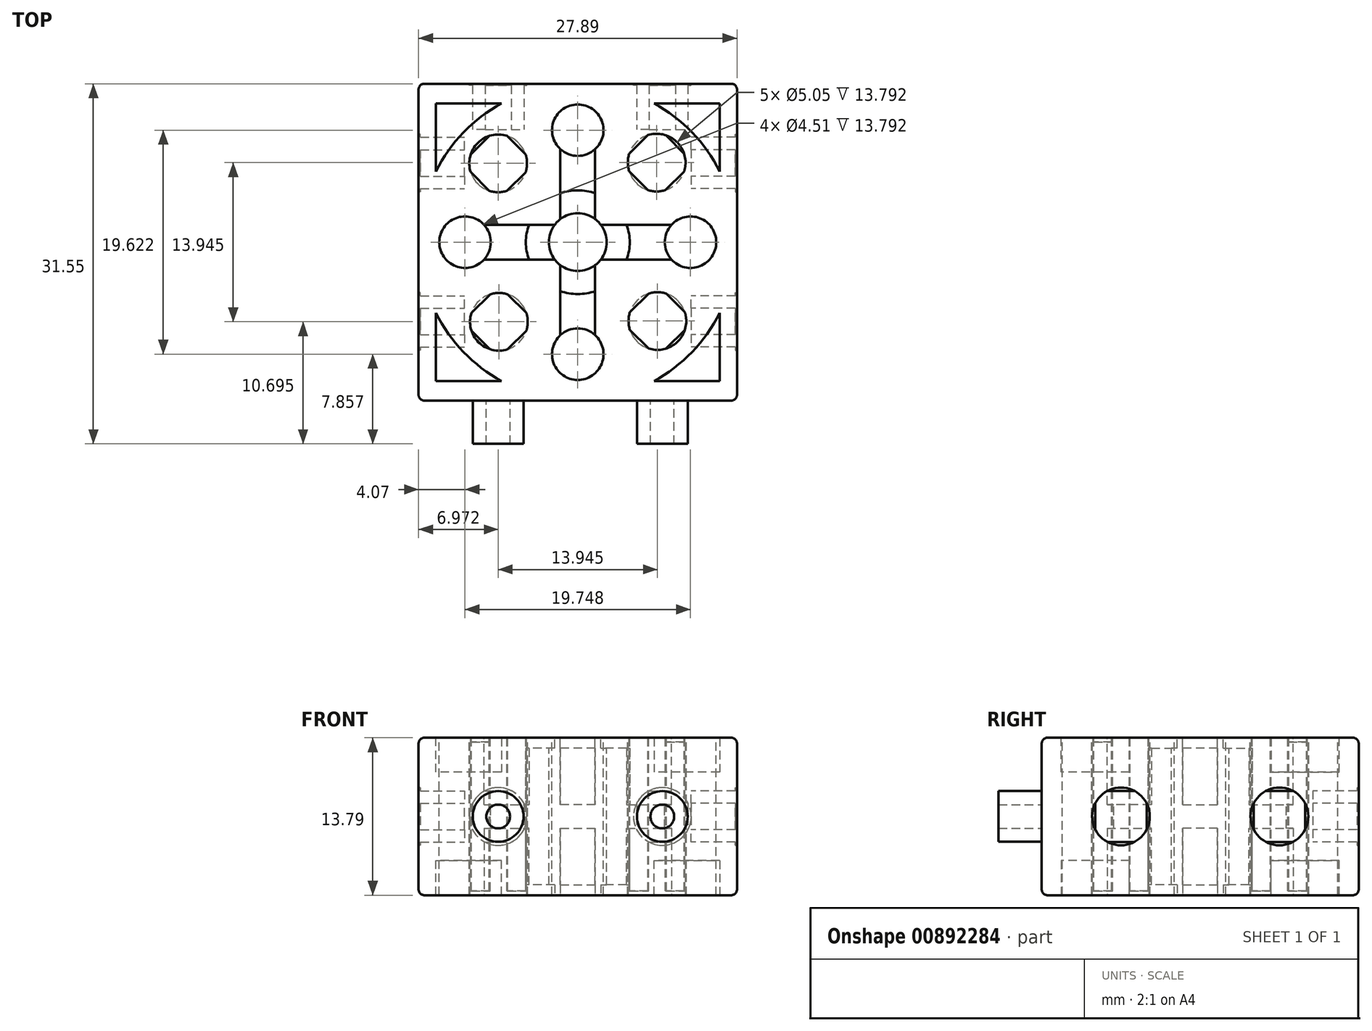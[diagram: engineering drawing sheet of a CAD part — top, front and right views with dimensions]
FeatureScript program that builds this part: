
annotation { "Feature Type Name" : "Feature", "Feature Type Description" : "" }
export const myFeature = defineFeature(function(context is Context, id is Id, definition is map)
    precondition{}
    {
        {
            var Q0;
            Q0=qCreatedBy(makeId("Top.planeOp"),FACE);
            var sketch = newSketch(context, id + "F0", { "sketchPlane" : qUnion([Q0])});
            skLineSegment(sketch, "E0.bottom", {"start": v(-12.61, 9.27) * mm, "end": v(15.28, 9.27) * mm});
            skLineSegment(sketch, "E0.top", {"start": v(-12.61, -18.5) * mm, "end": v(15.28, -18.5) * mm});
            skLineSegment(sketch, "E0.left", {"start": v(-12.61, 9.27) * mm, "end": v(-12.61, -18.5) * mm});
            skLineSegment(sketch, "E0.right", {"start": v(15.28, 9.27) * mm, "end": v(15.28, -18.5) * mm});
            skSolve(sketch);
        }
        {
            var Q0;
            Q0=qSketchRegion(id+"F0",true);
            extrude(context, id + "F1", {"entities" : qUnion([Q0]), "depth" : 13.8 * mm, "offsetDistance" : 25.4 * mm});
        }
        {
            var Q0;
            Q0=makeQuery(id+"F1.opExtrude","CAP_FACE",FACE,{"disambiguationData":[OSD([sQuery(id+"F0.wireOp",EDGE,"E0.bottom"),sQuery(id+"F0.wireOp",EDGE,"E0.top"),sQuery(id+"F0.wireOp",EDGE,"E0.left"),sQuery(id+"F0.wireOp",EDGE,"E0.right")])],"isStart":false});
            var sketch = newSketch(context, id + "F2", { "sketchPlane" : qUnion([Q0])});
            skLineSegment(sketch, "E1", {"start": v(1.33, 9.27) * mm, "end": v(1.33, -18.5) * mm, "construction": true});
            skLineSegment(sketch, "E2", {"start": v(-12.61, -4.61) * mm, "end": v(15.28, -4.61) * mm, "construction": true});
            skLineSegment(sketch, "E3.bottom", {"start": v(13.75, 7.56) * mm, "end": v(-11.09, 7.56) * mm});
            skLineSegment(sketch, "E3.top", {"start": v(13.75, -16.78) * mm, "end": v(-11.09, -16.78) * mm});
            skLineSegment(sketch, "E3.left", {"start": v(13.75, 7.56) * mm, "end": v(13.75, -16.78) * mm});
            skLineSegment(sketch, "E3.right", {"start": v(-11.09, 7.56) * mm, "end": v(-11.09, -16.78) * mm});
            skPoint(sketch, "E3.middle", {"position": v(1.33, -4.61) * mm});
            skSolve(sketch);
        }
        {
            var Q0;
            Q0=qSketchRegion(id+"F2",true);
            extrude(context, id + "F3", {"entities" : qUnion([Q0]), "operationType" : NewBodyOperationType.REMOVE, "oppositeDirection" : true, "depth" : 3.02 * mm, "offsetDistance" : 25.4 * mm});
        }
        {
            var Q0;
            Q0=makeQuery(id+"F1.opExtrude","CAP_FACE",FACE,{"disambiguationData":[OSD([sQuery(id+"F0.wireOp",EDGE,"E0.bottom"),sQuery(id+"F0.wireOp",EDGE,"E0.top"),sQuery(id+"F0.wireOp",EDGE,"E0.left"),sQuery(id+"F0.wireOp",EDGE,"E0.right")])],"isStart":true});
            var sketch = newSketch(context, id + "F4", { "sketchPlane" : qUnion([Q0])});
            skLineSegment(sketch, "E4.bottom", {"start": v(-11.09, -7.56) * mm, "end": v(13.75, -7.56) * mm});
            skLineSegment(sketch, "E4.top", {"start": v(-11.09, 16.78) * mm, "end": v(13.75, 16.78) * mm});
            skLineSegment(sketch, "E4.left", {"start": v(-11.09, -7.56) * mm, "end": v(-11.09, 16.78) * mm});
            skLineSegment(sketch, "E4.right", {"start": v(13.75, -7.56) * mm, "end": v(13.75, 16.78) * mm});
            skSolve(sketch);
        }
        {
            var Q0;
            Q0=makeQuery(id+"F4.imprint","IMPRINT",FACE,{"disambiguationData":[TD([[makeQuery(id+"F4.imprint","IMPRINT",EDGE,{"derivedFrom":sQuery(id+"F4.wireOp",EDGE,"E4.bottom")}),1.0]])]});
            extrude(context, id + "F5", {"entities" : qUnion([Q0]), "operationType" : NewBodyOperationType.REMOVE, "oppositeDirection" : true, "depth" : 3.02 * mm, "offsetDistance" : 25.4 * mm});
        }
        {
            var Q0;
            Q0=makeQuery(id+"F5.boolean.opBoolean","COPY",FACE,{"derivedFrom":makeQuery(id+"F5.opExtrude","CAP_FACE",FACE,{"disambiguationData":[OSD([sQuery(id+"F4.wireOp",EDGE,"E4.bottom"),sQuery(id+"F4.wireOp",EDGE,"E4.top"),sQuery(id+"F4.wireOp",EDGE,"E4.left"),sQuery(id+"F4.wireOp",EDGE,"E4.right")])],"isStart":false})});
            var sketch = newSketch(context, id + "F6", { "sketchPlane" : qUnion([Q0])});
            skCircle(sketch, "E5", {"center": v(1.33, 4.61) * mm, "radius": 13.88 * mm});
            skLineSegment(sketch, "E6", {"start": v(1.33, -7.56) * mm, "end": v(1.33, 16.78) * mm, "construction": true});
            skPoint(sketch, "E6.startSnap0", {"position": v(1.33, -7.56) * mm});
            skSolve(sketch);
        }
        {
            var Q0;
            {var subQ0=sQuery(id+"F6.wireOp",EDGE,"E5");var subQ1=makeQuery(id+"F5.boolean.opBoolean","COPY",EDGE,{"derivedFrom":makeQuery(id+"F5.opExtrude","CAP_EDGE",EDGE,{"disambiguationData":[OSD([sQuery(id+"F4.wireOp",EDGE,"E4.top")])],"isStart":false})});var subQ2=makeQuery(id+"F6.imprint","INTERSECT",VERTEX,{"disambiguationData":[OD(0.0)],"derivedFrom":[subQ1,subQ0]});Q0=makeQuery(id+"F6.imprint","IMPRINT",FACE,{"disambiguationData":[TD([[makeQuery(id+"F6.imprint","IMPRINT",EDGE,{"disambiguationData":[TD([[subQ2,-1.0]])],"derivedFrom":subQ0}),1.0]])]});}
            var Q1;
            {var subQ0=sQuery(id+"F6.wireOp",EDGE,"E5");var subQ1=makeQuery(id+"F5.boolean.opBoolean","COPY",EDGE,{"derivedFrom":makeQuery(id+"F5.opExtrude","CAP_EDGE",EDGE,{"disambiguationData":[OSD([sQuery(id+"F4.wireOp",EDGE,"E4.left")])],"isStart":false})});var subQ2=makeQuery(id+"F6.imprint","INTERSECT",VERTEX,{"disambiguationData":[OD(0.0)],"derivedFrom":[subQ1,subQ0]});Q1=makeQuery(id+"F6.imprint","IMPRINT",FACE,{"disambiguationData":[TD([[makeQuery(id+"F6.imprint","IMPRINT",EDGE,{"disambiguationData":[TD([[subQ2,-1.0]])],"derivedFrom":subQ0}),1.0]])]});}
            var Q2;
            {var subQ0=sQuery(id+"F6.wireOp",EDGE,"E5");var subQ1=makeQuery(id+"F5.boolean.opBoolean","COPY",EDGE,{"derivedFrom":makeQuery(id+"F5.opExtrude","CAP_EDGE",EDGE,{"disambiguationData":[OSD([sQuery(id+"F4.wireOp",EDGE,"E4.bottom")])],"isStart":false})});var subQ2=makeQuery(id+"F6.imprint","INTERSECT",VERTEX,{"disambiguationData":[OD(0.0)],"derivedFrom":[subQ1,subQ0]});Q2=makeQuery(id+"F6.imprint","IMPRINT",FACE,{"disambiguationData":[TD([[makeQuery(id+"F6.imprint","IMPRINT",EDGE,{"disambiguationData":[TD([[subQ2,-1.0]])],"derivedFrom":subQ0}),1.0]])]});}
            var Q3;
            {var subQ0=sQuery(id+"F6.wireOp",EDGE,"E5");var subQ1=makeQuery(id+"F5.boolean.opBoolean","COPY",EDGE,{"derivedFrom":makeQuery(id+"F5.opExtrude","CAP_EDGE",EDGE,{"disambiguationData":[OSD([sQuery(id+"F4.wireOp",EDGE,"E4.right")])],"isStart":false})});var subQ2=makeQuery(id+"F6.imprint","INTERSECT",VERTEX,{"disambiguationData":[OD(0.0)],"derivedFrom":[subQ1,subQ0]});Q3=makeQuery(id+"F6.imprint","IMPRINT",FACE,{"disambiguationData":[TD([[makeQuery(id+"F6.imprint","IMPRINT",EDGE,{"disambiguationData":[TD([[subQ2,1.0]])],"derivedFrom":subQ0}),1.0]])]});}
            var Q4;
            {var subQ0=sQuery(id+"F6.wireOp",EDGE,"E5");var subQ8=makeQuery(id+"F5.boolean.opBoolean","COPY",EDGE,{"derivedFrom":makeQuery(id+"F5.opExtrude","CAP_EDGE",EDGE,{"disambiguationData":[OSD([sQuery(id+"F4.wireOp",EDGE,"E4.top")])],"isStart":false})});var subQ11=makeQuery(id+"F6.imprint","INTERSECT",VERTEX,{"disambiguationData":[OD(0.0)],"derivedFrom":[subQ8,subQ0]});Q4=makeQuery(id+"F6.imprint","IMPRINT",FACE,{"disambiguationData":[TD([[makeQuery(id+"F6.imprint","IMPRINT",EDGE,{"disambiguationData":[TD([[subQ11,1.0]])],"derivedFrom":subQ0}),1.0]])]});}
            extrude(context, id + "F7", {"entities" : qUnion([Q0, Q1, Q2, Q3, Q4]), "operationType" : NewBodyOperationType.ADD, "depth" : 3.02 * mm, "offsetDistance" : 25.4 * mm});
        }
        {
            var Q0;
            Q0=makeQuery(id+"F3.boolean.opBoolean","COPY",FACE,{"derivedFrom":makeQuery(id+"F3.opExtrude","CAP_FACE",FACE,{"disambiguationData":[OSD([sQuery(id+"F2.wireOp",EDGE,"E3.bottom"),sQuery(id+"F2.wireOp",EDGE,"E3.top"),sQuery(id+"F2.wireOp",EDGE,"E3.left"),sQuery(id+"F2.wireOp",EDGE,"E3.right")])],"isStart":false})});
            var sketch = newSketch(context, id + "F8", { "sketchPlane" : qUnion([Q0])});
            skLineSegment(sketch, "E7", {"start": v(1.33, 7.56) * mm, "end": v(1.33, -16.78) * mm, "construction": true});
            skCircle(sketch, "E8", {"center": v(1.33, -4.61) * mm, "radius": 13.88 * mm});
            skSolve(sketch);
        }
        {
            var Q0;
            Q0=qSketchRegion(id+"F8",true);
            extrude(context, id + "F9", {"entities" : qUnion([Q0]), "operationType" : NewBodyOperationType.ADD, "depth" : 3.02 * mm, "offsetDistance" : 25.4 * mm});
        }
        {
            var Q0;
            Q0=makeQuery(id+"F9.boolean.opBoolean","MERGE",FACE,{"derivedFrom":[makeQuery(id+"F1.opExtrude","CAP_FACE",FACE,{"disambiguationData":[OSD([sQuery(id+"F0.wireOp",EDGE,"E0.bottom"),sQuery(id+"F0.wireOp",EDGE,"E0.top"),sQuery(id+"F0.wireOp",EDGE,"E0.left"),sQuery(id+"F0.wireOp",EDGE,"E0.right")])],"isStart":false}),makeQuery(id+"F9.opExtrude","CAP_FACE",FACE,{"disambiguationData":[OSD([sQuery(id+"F8.wireOp",EDGE,"E8")])],"isStart":false})]});
            var sketch = newSketch(context, id + "F10", { "sketchPlane" : qUnion([Q0])});
            skLineSegment(sketch, "E9", {"start": v(-12.61, -4.61) * mm, "end": v(15.28, -4.61) * mm, "construction": true});
            skLineSegment(sketch, "E10", {"start": v(1.33, 9.27) * mm, "end": v(1.33, -18.5) * mm, "construction": true});
            skCircle(sketch, "E11", {"center": v(1.33, -4.61) * mm, "radius": 2.53 * mm});
            skCircle(sketch, "E12", {"center": v(1.33, -14.42) * mm, "radius": 2.25 * mm});
            skCircle(sketch, "E13", {"center": v(1.33, 5.2) * mm, "radius": 2.25 * mm});
            skCircle(sketch, "E14", {"center": v(-8.54, -4.61) * mm, "radius": 2.25 * mm});
            skCircle(sketch, "E15", {"center": v(11.2, -4.61) * mm, "radius": 2.25 * mm});
            skCircle(sketch, "E16", {"center": v(-5.64, 2.3) * mm, "radius": 2.53 * mm});
            skCircle(sketch, "E17.1.0", {"center": v(-5.57, -11.58) * mm, "radius": 2.53 * mm});
            skCircle(sketch, "E17.2.0", {"center": v(8.3, -11.52) * mm, "radius": 2.53 * mm});
            skCircle(sketch, "E17.3.0", {"center": v(8.24, 2.36) * mm, "radius": 2.53 * mm});
            skSolve(sketch);
        }
        {
            var Q0;
            Q0=qSketchRegion(id+"F10",true);
            extrude(context, id + "F11", {"entities" : qUnion([Q0]), "operationType" : NewBodyOperationType.REMOVE, "oppositeDirection" : true, "depth" : 25.4 * mm, "offsetDistance" : 25.4 * mm});
        }
        {
            var Q0;
            Q0=makeQuery(id+"F9.boolean.opBoolean","MERGE",FACE,{"derivedFrom":[makeQuery(id+"F1.opExtrude","CAP_FACE",FACE,{"disambiguationData":[OSD([sQuery(id+"F0.wireOp",EDGE,"E0.bottom"),sQuery(id+"F0.wireOp",EDGE,"E0.top"),sQuery(id+"F0.wireOp",EDGE,"E0.left"),sQuery(id+"F0.wireOp",EDGE,"E0.right")])],"isStart":false}),makeQuery(id+"F9.opExtrude","CAP_FACE",FACE,{"disambiguationData":[OSD([sQuery(id+"F8.wireOp",EDGE,"E8")])],"isStart":false})]});
            var sketch = newSketch(context, id + "F12", { "sketchPlane" : qUnion([Q0])});
            skLineSegment(sketch, "E18", {"start": v(-12.61, -4.61) * mm, "end": v(15.28, -4.61) * mm, "construction": true});
            skLineSegment(sketch, "E19", {"start": v(1.33, 9.27) * mm, "end": v(1.33, -18.5) * mm, "construction": true});
            skLineSegment(sketch, "E20", {"start": v(-6.88, -3.09) * mm, "end": v(9.55, -3.09) * mm});
            skLineSegment(sketch, "E21", {"start": v(-6.88, -6.14) * mm, "end": v(9.55, -6.14) * mm});
            skLineSegment(sketch, "E22", {"start": v(-0.19, 3.54) * mm, "end": v(-0.19, -12.76) * mm});
            skLineSegment(sketch, "E23", {"start": v(2.86, -12.76) * mm, "end": v(2.86, 3.54) * mm});
            skLineSegment(sketch, "E24", {"start": v(-0.19, -7.96) * mm, "end": v(2.86, -7.96) * mm, "construction": true});
            skPoint(sketch, "E25", {"position": v(1.33, -7.96) * mm});
            skLineSegment(sketch, "E26", {"start": v(-2, -3.09) * mm, "end": v(-2, -6.14) * mm, "construction": true});
            skPoint(sketch, "E27", {"position": v(-2, -4.61) * mm});
            skSolve(sketch);
        }
        {
            var Q0;
            {var subQ0=sQuery(id+"F12.wireOp",EDGE,"E22");var subQ1=makeQuery(id+"F11.boolean.opBoolean","COPY",EDGE,{"derivedFrom":makeQuery(id+"F11.opExtrude","CAP_EDGE",EDGE,{"disambiguationData":[OSD([sQuery(id+"F10.wireOp",EDGE,"E13")])],"isStart":true})});var subQ2=makeQuery(id+"F12.imprint","INTERSECT",VERTEX,{"derivedFrom":[subQ1,subQ0]});Q0=makeQuery(id+"F12.imprint","IMPRINT",FACE,{"disambiguationData":[TD([[makeQuery(id+"F12.imprint","IMPRINT",EDGE,{"disambiguationData":[TD([[subQ2,-1.0]])],"derivedFrom":subQ0}),1.0]])]});}
            var Q1;
            {var subQ0=sQuery(id+"F12.wireOp",EDGE,"E22");var subQ1=makeQuery(id+"F11.boolean.opBoolean","COPY",EDGE,{"derivedFrom":makeQuery(id+"F11.opExtrude","CAP_EDGE",EDGE,{"disambiguationData":[OSD([sQuery(id+"F10.wireOp",EDGE,"E12")])],"isStart":true})});var subQ2=makeQuery(id+"F12.imprint","INTERSECT",VERTEX,{"derivedFrom":[subQ1,subQ0]});Q1=makeQuery(id+"F12.imprint","IMPRINT",FACE,{"disambiguationData":[TD([[makeQuery(id+"F12.imprint","IMPRINT",EDGE,{"disambiguationData":[TD([[subQ2,1.0]])],"derivedFrom":subQ0}),1.0]])]});}
            var Q2;
            {var subQ0=sQuery(id+"F12.wireOp",EDGE,"E20");var subQ1=makeQuery(id+"F11.boolean.opBoolean","COPY",EDGE,{"derivedFrom":makeQuery(id+"F11.opExtrude","CAP_EDGE",EDGE,{"disambiguationData":[OSD([sQuery(id+"F10.wireOp",EDGE,"E14")])],"isStart":true})});var subQ2=makeQuery(id+"F12.imprint","INTERSECT",VERTEX,{"derivedFrom":[subQ1,subQ0]});Q2=makeQuery(id+"F12.imprint","IMPRINT",FACE,{"disambiguationData":[TD([[makeQuery(id+"F12.imprint","IMPRINT",EDGE,{"disambiguationData":[TD([[subQ2,-1.0]])],"derivedFrom":subQ0}),-1.0]])]});}
            var Q3;
            {var subQ0=sQuery(id+"F12.wireOp",EDGE,"E20");var subQ1=makeQuery(id+"F11.boolean.opBoolean","COPY",EDGE,{"derivedFrom":makeQuery(id+"F11.opExtrude","CAP_EDGE",EDGE,{"disambiguationData":[OSD([sQuery(id+"F10.wireOp",EDGE,"E15")])],"isStart":true})});var subQ2=makeQuery(id+"F12.imprint","INTERSECT",VERTEX,{"derivedFrom":[subQ1,subQ0]});Q3=makeQuery(id+"F12.imprint","IMPRINT",FACE,{"disambiguationData":[TD([[makeQuery(id+"F12.imprint","IMPRINT",EDGE,{"disambiguationData":[TD([[subQ2,1.0]])],"derivedFrom":subQ0}),-1.0]])]});}
            extrude(context, id + "F13", {"entities" : qUnion([Q0, Q1, Q2, Q3]), "operationType" : NewBodyOperationType.REMOVE, "oppositeDirection" : true, "depth" : 5.87 * mm, "offsetDistance" : 25.4 * mm});
        }
        {
            var Q0;
            Q0=makeQuery(id+"F7.boolean.opBoolean","MERGE",FACE,{"derivedFrom":[makeQuery(id+"F1.opExtrude","CAP_FACE",FACE,{"disambiguationData":[OSD([sQuery(id+"F0.wireOp",EDGE,"E0.bottom"),sQuery(id+"F0.wireOp",EDGE,"E0.top"),sQuery(id+"F0.wireOp",EDGE,"E0.left"),sQuery(id+"F0.wireOp",EDGE,"E0.right")])],"isStart":true}),makeQuery(id+"F7.opExtrude","CAP_FACE",FACE,{"disambiguationData":[OSD([sQuery(id+"F6.wireOp",EDGE,"E5")])],"isStart":false})]});
            var sketch = newSketch(context, id + "F14", { "sketchPlane" : qUnion([Q0])});
            skLineSegment(sketch, "E28.0", {"start": v(2.86, 12.76) * mm, "end": v(2.86, 6.63) * mm});
            skLineSegment(sketch, "E28.1", {"start": v(3.35, 6.14) * mm, "end": v(9.55, 6.14) * mm});
            skLineSegment(sketch, "E28.2", {"start": v(3.35, 3.09) * mm, "end": v(9.55, 3.09) * mm});
            skLineSegment(sketch, "E28.3", {"start": v(2.86, 2.6) * mm, "end": v(2.86, -3.54) * mm});
            skLineSegment(sketch, "E28.4", {"start": v(-0.19, -3.54) * mm, "end": v(-0.19, 2.6) * mm});
            skLineSegment(sketch, "E28.5", {"start": v(-0.19, 6.63) * mm, "end": v(-0.19, 12.76) * mm});
            skLineSegment(sketch, "E28.6", {"start": v(-6.88, 6.14) * mm, "end": v(-0.68, 6.14) * mm});
            skLineSegment(sketch, "E28.7", {"start": v(-6.88, 3.09) * mm, "end": v(-0.68, 3.09) * mm});
            skSolve(sketch);
        }
        {
            var Q0;
            {var subQ0=sQuery(id+"F14.wireOp",EDGE,"E28.6");Q0=makeQuery(id+"F14.imprint","IMPRINT",FACE,{"disambiguationData":[TD([[makeQuery(id+"F14.imprint","IMPRINT",EDGE,{"derivedFrom":subQ0}),-1.0]])]});}
            var Q1;
            {var subQ0=sQuery(id+"F14.wireOp",EDGE,"E28.3");Q1=makeQuery(id+"F14.imprint","IMPRINT",FACE,{"disambiguationData":[TD([[makeQuery(id+"F14.imprint","IMPRINT",EDGE,{"derivedFrom":subQ0}),-1.0]])]});}
            var Q2;
            {var subQ0=sQuery(id+"F14.wireOp",EDGE,"E28.0");Q2=makeQuery(id+"F14.imprint","IMPRINT",FACE,{"disambiguationData":[TD([[makeQuery(id+"F14.imprint","IMPRINT",EDGE,{"derivedFrom":subQ0}),-1.0]])]});}
            var Q3;
            {var subQ0=sQuery(id+"F14.wireOp",EDGE,"E28.1");Q3=makeQuery(id+"F14.imprint","IMPRINT",FACE,{"disambiguationData":[TD([[makeQuery(id+"F14.imprint","IMPRINT",EDGE,{"derivedFrom":subQ0}),-1.0]])]});}
            extrude(context, id + "F15", {"entities" : qUnion([Q0, Q1, Q2, Q3]), "operationType" : NewBodyOperationType.REMOVE, "oppositeDirection" : true, "depth" : 5.87 * mm, "offsetDistance" : 25.4 * mm});
        }
        {
            var Q0;
            Q0=makeQuery(id+"F15.boolean.opBoolean","COPY",FACE,{"derivedFrom":makeQuery(id+"F15.opExtrude","CAP_FACE",FACE,{"disambiguationData":[OSD([sQuery(id+"F0.wireOp",EDGE,"E0.bottom"),sQuery(id+"F0.wireOp",EDGE,"E0.top"),sQuery(id+"F0.wireOp",EDGE,"E0.left"),sQuery(id+"F0.wireOp",EDGE,"E0.right"),sQuery(id+"F6.wireOp",EDGE,"E5"),sQuery(id+"F10.wireOp",EDGE,"E11"),sQuery(id+"F10.wireOp",EDGE,"E13"),sQuery(id+"F14.wireOp",EDGE,"E28.3"),sQuery(id+"F14.wireOp",EDGE,"E28.4")])],"isStart":false})});
            var sketch = newSketch(context, id + "F16", { "sketchPlane" : qUnion([Q0])});
            skCircle(sketch, "E29", {"center": v(1.33, 4.61) * mm, "radius": 4.55 * mm});
            skCircle(sketch, "E30", {"center": v(1.33, 4.61) * mm, "radius": 2.53 * mm});
            skSolve(sketch);
        }
        {
            var Q0;
            {var subQ5=sQuery(id+"F16.wireOp",EDGE,"E30");Q0=makeQuery(id+"F16.imprint","IMPRINT",FACE,{"disambiguationData":[TD([[makeQuery(id+"F16.imprint","IMPRINT",EDGE,{"disambiguationData":[OD(1.0)],"derivedFrom":subQ5}),-1.0]])]});}
            var Q1;
            {var subQ5=sQuery(id+"F16.wireOp",EDGE,"E30");Q1=makeQuery(id+"F16.imprint","IMPRINT",FACE,{"disambiguationData":[TD([[makeQuery(id+"F16.imprint","IMPRINT",EDGE,{"disambiguationData":[OD(0.0)],"derivedFrom":subQ5}),1.0]])]});}
            extrude(context, id + "F17", {"entities" : qUnion([Q0, Q1]), "operationType" : NewBodyOperationType.ADD, "depth" : 4.95 * mm, "offsetDistance" : 25.4 * mm});
        }
        {
            var Q0;
            Q0=makeQuery(id+"F13.boolean.opBoolean","COPY",FACE,{"derivedFrom":makeQuery(id+"F13.opExtrude","CAP_FACE",FACE,{"disambiguationData":[OSD([sQuery(id+"F10.wireOp",EDGE,"E11"),sQuery(id+"F10.wireOp",EDGE,"E12"),sQuery(id+"F12.wireOp",EDGE,"E22"),sQuery(id+"F12.wireOp",EDGE,"E23")])],"isStart":false})});
            var sketch = newSketch(context, id + "F18", { "sketchPlane" : qUnion([Q0])});
            skCircle(sketch, "E31", {"center": v(1.33, -4.61) * mm, "radius": 4.55 * mm});
            skCircle(sketch, "E32", {"center": v(1.33, -4.61) * mm, "radius": 2.53 * mm});
            skSolve(sketch);
        }
        {
            var Q0;
            {var subQ0=sQuery(id+"F18.wireOp",EDGE,"E31");var subQ1=sQuery(id+"F12.wireOp",EDGE,"E22");var subQ2=makeQuery(id+"F11.boolean.opBoolean","COPY",EDGE,{"derivedFrom":makeQuery(id+"F11.opExtrude","CAP_EDGE",EDGE,{"disambiguationData":[OSD([sQuery(id+"F10.wireOp",EDGE,"E12")])],"isStart":true})});var subQ4=makeQuery(id+"F13.boolean.opBoolean","COPY",EDGE,{"derivedFrom":makeQuery(id+"F13.opExtrude","CAP_EDGE",EDGE,{"disambiguationData":[OSD([subQ1]),TDD([makeQuery(id+"F12.imprint","IMPRINT",EDGE,{"disambiguationData":[TD([[makeQuery(id+"F12.imprint","INTERSECT",VERTEX,{"derivedFrom":[subQ2,subQ1]}),1.0]])],"derivedFrom":subQ1})])],"isStart":false})});var subQ5=makeQuery(id+"F18.imprint","INTERSECT",VERTEX,{"derivedFrom":[subQ4,subQ0]});Q0=makeQuery(id+"F18.imprint","IMPRINT",FACE,{"disambiguationData":[TD([[makeQuery(id+"F18.imprint","IMPRINT",EDGE,{"disambiguationData":[TD([[subQ5,1.0]])],"derivedFrom":subQ0}),1.0]])]});}
            var Q1;
            {var subQ0=sQuery(id+"F18.wireOp",EDGE,"E31");var subQ1=sQuery(id+"F12.wireOp",EDGE,"E22");var subQ2=makeQuery(id+"F11.boolean.opBoolean","COPY",EDGE,{"derivedFrom":makeQuery(id+"F11.opExtrude","CAP_EDGE",EDGE,{"disambiguationData":[OSD([sQuery(id+"F10.wireOp",EDGE,"E12")])],"isStart":true})});var subQ4=makeQuery(id+"F13.boolean.opBoolean","COPY",EDGE,{"derivedFrom":makeQuery(id+"F13.opExtrude","CAP_EDGE",EDGE,{"disambiguationData":[OSD([subQ1]),TDD([makeQuery(id+"F12.imprint","IMPRINT",EDGE,{"disambiguationData":[TD([[makeQuery(id+"F12.imprint","INTERSECT",VERTEX,{"derivedFrom":[subQ2,subQ1]}),1.0]])],"derivedFrom":subQ1})])],"isStart":false})});var subQ5=makeQuery(id+"F18.imprint","INTERSECT",VERTEX,{"derivedFrom":[subQ4,subQ0]});Q1=makeQuery(id+"F18.imprint","IMPRINT",FACE,{"disambiguationData":[TD([[makeQuery(id+"F18.imprint","IMPRINT",EDGE,{"disambiguationData":[TD([[subQ5,-1.0]])],"derivedFrom":subQ0}),1.0]])]});}
            extrude(context, id + "F19", {"entities" : qUnion([Q0, Q1]), "operationType" : NewBodyOperationType.ADD, "depth" : 4.95 * mm, "offsetDistance" : 25.4 * mm});
        }
        {
            var Q0;
            Q0=makeQuery(id+"F1.opExtrude","SWEPT_FACE",FACE,{"disambiguationData":[OSD([sQuery(id+"F0.wireOp",EDGE,"E0.top")])]});
            var sketch = newSketch(context, id + "F20", { "sketchPlane" : qUnion([Q0])});
            skLineSegment(sketch, "E33", {"start": v(15.28, 6.9) * mm, "end": v(-12.61, 6.9) * mm, "construction": true});
            skCircle(sketch, "E34", {"center": v(8.74, 6.9) * mm, "radius": 2.22 * mm});
            skCircle(sketch, "E35", {"center": v(-5.64, 6.9) * mm, "radius": 2.22 * mm});
            skLineSegment(sketch, "E36", {"start": v(1.33, 0) * mm, "end": v(1.33, 13.8) * mm, "construction": true});
            skPoint(sketch, "E37", {"position": v(1.33, 6.9) * mm});
            skLineSegment(sketch, "E38", {"start": v(1.33, 0) * mm, "end": v(15.28, 0) * mm, "construction": true});
            skLineSegment(sketch, "E39", {"start": v(15.28, 0) * mm, "end": v(8.3, 0) * mm});
            skLineSegment(sketch, "E40", {"start": v(8.3, 0) * mm, "end": v(8.3, 13.8) * mm, "construction": true});
            skLineSegment(sketch, "E41", {"start": v(1.33, 0) * mm, "end": v(-12.61, 0) * mm, "construction": true});
            skLineSegment(sketch, "E42", {"start": v(-5.64, 0) * mm, "end": v(-5.64, 13.8) * mm, "construction": true});
            skCircle(sketch, "E43", {"center": v(8.74, 6.9) * mm, "radius": 1.04 * mm});
            skCircle(sketch, "E44", {"center": v(-5.64, 6.9) * mm, "radius": 1.04 * mm});
            skSolve(sketch);
        }
        {
            var Q0;
            Q0=makeQuery(id+"F20.imprint","IMPRINT",FACE,{"disambiguationData":[TD([[makeQuery(id+"F20.imprint","IMPRINT",EDGE,{"derivedFrom":sQuery(id+"F20.wireOp",EDGE,"E34")}),1.0]])]});
            var Q1;
            Q1=makeQuery(id+"F20.imprint","IMPRINT",FACE,{"disambiguationData":[TD([[makeQuery(id+"F20.imprint","IMPRINT",EDGE,{"derivedFrom":sQuery(id+"F20.wireOp",EDGE,"E35")}),1.0]])]});
            extrude(context, id + "F21", {"entities" : qUnion([Q0, Q1]), "operationType" : NewBodyOperationType.ADD, "depth" : 3.78 * mm, "offsetDistance" : 25.4 * mm});
        }
        {
            var Q0;
            Q0=makeQuery(id+"F1.opExtrude","SWEPT_FACE",FACE,{"disambiguationData":[OSD([sQuery(id+"F0.wireOp",EDGE,"E0.bottom")])]});
            var sketch = newSketch(context, id + "F22", { "sketchPlane" : qUnion([Q0])});
            skCircle(sketch, "E45.0", {"center": v(-8.74, 6.9) * mm, "radius": 2.22 * mm, "construction": true});
            skCircle(sketch, "E45.1", {"center": v(5.64, 6.9) * mm, "radius": 2.22 * mm, "construction": true});
            skCircle(sketch, "E46", {"center": v(-8.74, 6.9) * mm, "radius": 2.53 * mm});
            skCircle(sketch, "E47", {"center": v(5.64, 6.9) * mm, "radius": 2.53 * mm});
            skSolve(sketch);
        }
        {
            var Q0;
            Q0=qSketchRegion(id+"F22",true);
            extrude(context, id + "F23", {"entities" : qUnion([Q0]), "operationType" : NewBodyOperationType.REMOVE, "oppositeDirection" : true, "depth" : 4 * mm, "offsetDistance" : 25.4 * mm});
        }
        {
            var Q0;
            Q0=makeQuery(id+"F1.opExtrude","SWEPT_FACE",FACE,{"disambiguationData":[OSD([sQuery(id+"F0.wireOp",EDGE,"E0.right")])]});
            var sketch = newSketch(context, id + "F24", { "sketchPlane" : qUnion([Q0])});
            skLineSegment(sketch, "E48", {"start": v(9.27, 6.9) * mm, "end": v(-18.5, 6.9) * mm, "construction": true});
            skLineSegment(sketch, "E49", {"start": v(-4.61, 13.8) * mm, "end": v(-4.61, 0) * mm});
            skLineSegment(sketch, "E50", {"start": v(-4.61, 13.8) * mm, "end": v(9.27, 13.8) * mm, "construction": true});
            skLineSegment(sketch, "E51", {"start": v(-4.61, 13.8) * mm, "end": v(-18.5, 13.8) * mm, "construction": true});
            skLineSegment(sketch, "E52", {"start": v(-11.55, 13.8) * mm, "end": v(-11.55, 0) * mm, "construction": true});
            skLineSegment(sketch, "E53", {"start": v(2.33, 13.8) * mm, "end": v(2.33, 0) * mm, "construction": true});
            skPoint(sketch, "E54", {"position": v(-11.55, 6.9) * mm});
            skPoint(sketch, "E55", {"position": v(2.33, 6.9) * mm});
            skCircle(sketch, "E56", {"center": v(-11.55, 6.9) * mm, "radius": 2.53 * mm});
            skCircle(sketch, "E57", {"center": v(2.33, 6.9) * mm, "radius": 2.53 * mm});
            skSolve(sketch);
        }
        {
            var Q0;
            Q0=qSketchRegion(id+"F24",true);
            extrude(context, id + "F25", {"entities" : qUnion([Q0]), "operationType" : NewBodyOperationType.REMOVE, "oppositeDirection" : true, "depth" : 4 * mm, "offsetDistance" : 25.4 * mm});
        }
        {
            var Q0;
            Q0=makeQuery(id+"F1.opExtrude","SWEPT_FACE",FACE,{"disambiguationData":[OSD([sQuery(id+"F0.wireOp",EDGE,"E0.left")])]});
            var sketch = newSketch(context, id + "F26", { "sketchPlane" : qUnion([Q0])});
            skCircle(sketch, "E58.0", {"center": v(-2.33, 6.9) * mm, "radius": 2.53 * mm});
            skCircle(sketch, "E58.1", {"center": v(11.55, 6.9) * mm, "radius": 2.53 * mm});
            skSolve(sketch);
        }
        {
            var Q0;
            Q0=qSketchRegion(id+"F26",true);
            extrude(context, id + "F27", {"entities" : qUnion([Q0]), "operationType" : NewBodyOperationType.REMOVE, "oppositeDirection" : true, "depth" : 4 * mm, "offsetDistance" : 25.4 * mm});
        }
        {
            var Q0;
            Q0=makeQuery(id+"F23.boolean.opBoolean","COPY",FACE,{"derivedFrom":makeQuery(id+"F23.opExtrude","CAP_FACE",FACE,{"disambiguationData":[OSD([sQuery(id+"F22.wireOp",EDGE,"E46")])],"isStart":false})});
            var sketch = newSketch(context, id + "F28", { "sketchPlane" : qUnion([Q0])});
            skLineSegment(sketch, "E59.bottom", {"start": v(-6.5, 9.14) * mm, "end": v(-10.99, 9.14) * mm});
            skLineSegment(sketch, "E59.top", {"start": v(-6.5, 4.65) * mm, "end": v(-10.99, 4.65) * mm});
            skLineSegment(sketch, "E59.left", {"start": v(-6.5, 9.14) * mm, "end": v(-6.5, 4.65) * mm});
            skLineSegment(sketch, "E59.right", {"start": v(-10.99, 9.14) * mm, "end": v(-10.99, 4.65) * mm});
            skPoint(sketch, "E59.middle", {"position": v(-8.74, 6.9) * mm});
            skLineSegment(sketch, "E60.bottom", {"start": v(7.89, 9.14) * mm, "end": v(3.4, 9.14) * mm});
            skLineSegment(sketch, "E60.top", {"start": v(7.89, 4.65) * mm, "end": v(3.4, 4.65) * mm});
            skLineSegment(sketch, "E60.left", {"start": v(7.89, 9.14) * mm, "end": v(7.89, 4.65) * mm});
            skLineSegment(sketch, "E60.right", {"start": v(3.4, 9.14) * mm, "end": v(3.4, 4.65) * mm});
            skPoint(sketch, "E60.middle", {"position": v(5.64, 6.9) * mm});
            skCircle(sketch, "E61.0", {"center": v(-8.74, 6.9) * mm, "radius": 2.53 * mm});
            skCircle(sketch, "E62.0", {"center": v(5.64, 6.9) * mm, "radius": 2.53 * mm});
            skSolve(sketch);
        }
        {
            var Q0;
            {var subQ0=sQuery(id+"F28.wireOp",EDGE,"E61.0");var subQ1=sQuery(id+"F28.wireOp",EDGE,"E59.right");var subQ2=makeQuery(id+"F28.imprint","INTERSECT",VERTEX,{"disambiguationData":[OD(0.0)],"derivedFrom":[subQ1,subQ0]});Q0=makeQuery(id+"F28.imprint","IMPRINT",FACE,{"disambiguationData":[TD([[makeQuery(id+"F28.imprint","IMPRINT",EDGE,{"disambiguationData":[TD([[subQ2,-1.0]])],"derivedFrom":subQ1}),-1.0]])]});}
            var Q1;
            {var subQ0=sQuery(id+"F28.wireOp",EDGE,"E61.0");var subQ1=sQuery(id+"F28.wireOp",EDGE,"E59.top");var subQ2=makeQuery(id+"F28.imprint","INTERSECT",VERTEX,{"disambiguationData":[OD(0.0)],"derivedFrom":[subQ1,subQ0]});Q1=makeQuery(id+"F28.imprint","IMPRINT",FACE,{"disambiguationData":[TD([[makeQuery(id+"F28.imprint","IMPRINT",EDGE,{"disambiguationData":[TD([[subQ2,-1.0]])],"derivedFrom":subQ1}),1.0]])]});}
            var Q2;
            {var subQ0=sQuery(id+"F28.wireOp",EDGE,"E61.0");var subQ1=sQuery(id+"F28.wireOp",EDGE,"E59.left");var subQ2=makeQuery(id+"F28.imprint","INTERSECT",VERTEX,{"disambiguationData":[OD(0.0)],"derivedFrom":[subQ1,subQ0]});Q2=makeQuery(id+"F28.imprint","IMPRINT",FACE,{"disambiguationData":[TD([[makeQuery(id+"F28.imprint","IMPRINT",EDGE,{"disambiguationData":[TD([[subQ2,-1.0]])],"derivedFrom":subQ1}),1.0]])]});}
            var Q3;
            {var subQ0=sQuery(id+"F28.wireOp",EDGE,"E61.0");var subQ1=sQuery(id+"F28.wireOp",EDGE,"E59.bottom");var subQ2=makeQuery(id+"F28.imprint","INTERSECT",VERTEX,{"disambiguationData":[OD(0.0)],"derivedFrom":[subQ1,subQ0]});Q3=makeQuery(id+"F28.imprint","IMPRINT",FACE,{"disambiguationData":[TD([[makeQuery(id+"F28.imprint","IMPRINT",EDGE,{"disambiguationData":[TD([[subQ2,-1.0]])],"derivedFrom":subQ1}),-1.0]])]});}
            var Q4;
            {var subQ0=sQuery(id+"F28.wireOp",EDGE,"E62.0");var subQ1=sQuery(id+"F28.wireOp",EDGE,"E60.bottom");var subQ2=makeQuery(id+"F28.imprint","INTERSECT",VERTEX,{"disambiguationData":[OD(0.0)],"derivedFrom":[subQ1,subQ0]});Q4=makeQuery(id+"F28.imprint","IMPRINT",FACE,{"disambiguationData":[TD([[makeQuery(id+"F28.imprint","IMPRINT",EDGE,{"disambiguationData":[TD([[subQ2,-1.0]])],"derivedFrom":subQ1}),-1.0]])]});}
            var Q5;
            {var subQ0=sQuery(id+"F28.wireOp",EDGE,"E62.0");var subQ1=sQuery(id+"F28.wireOp",EDGE,"E60.left");var subQ2=makeQuery(id+"F28.imprint","INTERSECT",VERTEX,{"disambiguationData":[OD(0.0)],"derivedFrom":[subQ1,subQ0]});Q5=makeQuery(id+"F28.imprint","IMPRINT",FACE,{"disambiguationData":[TD([[makeQuery(id+"F28.imprint","IMPRINT",EDGE,{"disambiguationData":[TD([[subQ2,-1.0]])],"derivedFrom":subQ1}),1.0]])]});}
            var Q6;
            {var subQ0=sQuery(id+"F28.wireOp",EDGE,"E62.0");var subQ1=sQuery(id+"F28.wireOp",EDGE,"E60.right");var subQ2=makeQuery(id+"F28.imprint","INTERSECT",VERTEX,{"disambiguationData":[OD(0.0)],"derivedFrom":[subQ1,subQ0]});Q6=makeQuery(id+"F28.imprint","IMPRINT",FACE,{"disambiguationData":[TD([[makeQuery(id+"F28.imprint","IMPRINT",EDGE,{"disambiguationData":[TD([[subQ2,-1.0]])],"derivedFrom":subQ1}),-1.0]])]});}
            var Q7;
            {var subQ0=sQuery(id+"F28.wireOp",EDGE,"E62.0");var subQ1=sQuery(id+"F28.wireOp",EDGE,"E60.top");var subQ2=makeQuery(id+"F28.imprint","INTERSECT",VERTEX,{"disambiguationData":[OD(0.0)],"derivedFrom":[subQ1,subQ0]});Q7=makeQuery(id+"F28.imprint","IMPRINT",FACE,{"disambiguationData":[TD([[makeQuery(id+"F28.imprint","IMPRINT",EDGE,{"disambiguationData":[TD([[subQ2,-1.0]])],"derivedFrom":subQ1}),1.0]])]});}
            extrude(context, id + "F29", {"entities" : qUnion([Q0, Q1, Q2, Q3, Q4, Q5, Q6, Q7]), "operationType" : NewBodyOperationType.ADD, "depth" : 3.86 * mm, "offsetDistance" : 25.4 * mm});
        }
        {
            var Q0;
            Q0=makeQuery(id+"F25.boolean.opBoolean","COPY",FACE,{"derivedFrom":makeQuery(id+"F25.opExtrude","CAP_FACE",FACE,{"disambiguationData":[OSD([sQuery(id+"F24.wireOp",EDGE,"E56")])],"isStart":false})});
            var sketch = newSketch(context, id + "F30", { "sketchPlane" : qUnion([Q0])});
            skLineSegment(sketch, "E63.bottom", {"start": v(-9.3, 9.14) * mm, "end": v(-13.8, 9.14) * mm});
            skLineSegment(sketch, "E63.top", {"start": v(-9.3, 4.65) * mm, "end": v(-13.8, 4.65) * mm});
            skLineSegment(sketch, "E63.left", {"start": v(-9.3, 9.14) * mm, "end": v(-9.3, 4.65) * mm});
            skLineSegment(sketch, "E63.right", {"start": v(-13.8, 9.14) * mm, "end": v(-13.8, 4.65) * mm});
            skPoint(sketch, "E63.middle", {"position": v(-11.55, 6.9) * mm});
            skLineSegment(sketch, "E64.bottom", {"start": v(4.58, 9.14) * mm, "end": v(0.08, 9.14) * mm});
            skLineSegment(sketch, "E64.top", {"start": v(4.58, 4.65) * mm, "end": v(0.08, 4.65) * mm});
            skLineSegment(sketch, "E64.left", {"start": v(4.58, 9.14) * mm, "end": v(4.58, 4.65) * mm});
            skLineSegment(sketch, "E64.right", {"start": v(0.08, 9.14) * mm, "end": v(0.08, 4.65) * mm});
            skPoint(sketch, "E64.middle", {"position": v(2.33, 6.9) * mm});
            skCircle(sketch, "E65.0", {"center": v(-11.55, 6.9) * mm, "radius": 2.53 * mm});
            skCircle(sketch, "E65.1", {"center": v(2.33, 6.9) * mm, "radius": 2.53 * mm});
            skSolve(sketch);
        }
        {
            var Q0;
            {var subQ0=sQuery(id+"F30.wireOp",EDGE,"E65.0");var subQ1=sQuery(id+"F30.wireOp",EDGE,"E63.bottom");var subQ2=makeQuery(id+"F30.imprint","INTERSECT",VERTEX,{"disambiguationData":[OD(0.0)],"derivedFrom":[subQ1,subQ0]});Q0=makeQuery(id+"F30.imprint","IMPRINT",FACE,{"disambiguationData":[TD([[makeQuery(id+"F30.imprint","IMPRINT",EDGE,{"disambiguationData":[TD([[subQ2,-1.0]])],"derivedFrom":subQ1}),-1.0]])]});}
            var Q1;
            {var subQ0=sQuery(id+"F30.wireOp",EDGE,"E65.0");var subQ1=sQuery(id+"F30.wireOp",EDGE,"E63.right");var subQ2=makeQuery(id+"F30.imprint","INTERSECT",VERTEX,{"disambiguationData":[OD(0.0)],"derivedFrom":[subQ1,subQ0]});Q1=makeQuery(id+"F30.imprint","IMPRINT",FACE,{"disambiguationData":[TD([[makeQuery(id+"F30.imprint","IMPRINT",EDGE,{"disambiguationData":[TD([[subQ2,-1.0]])],"derivedFrom":subQ1}),-1.0]])]});}
            var Q2;
            {var subQ0=sQuery(id+"F30.wireOp",EDGE,"E65.0");var subQ1=sQuery(id+"F30.wireOp",EDGE,"E63.left");var subQ2=makeQuery(id+"F30.imprint","INTERSECT",VERTEX,{"disambiguationData":[OD(0.0)],"derivedFrom":[subQ1,subQ0]});Q2=makeQuery(id+"F30.imprint","IMPRINT",FACE,{"disambiguationData":[TD([[makeQuery(id+"F30.imprint","IMPRINT",EDGE,{"disambiguationData":[TD([[subQ2,-1.0]])],"derivedFrom":subQ1}),1.0]])]});}
            var Q3;
            {var subQ0=sQuery(id+"F30.wireOp",EDGE,"E65.0");var subQ1=sQuery(id+"F30.wireOp",EDGE,"E63.top");var subQ2=makeQuery(id+"F30.imprint","INTERSECT",VERTEX,{"disambiguationData":[OD(0.0)],"derivedFrom":[subQ1,subQ0]});Q3=makeQuery(id+"F30.imprint","IMPRINT",FACE,{"disambiguationData":[TD([[makeQuery(id+"F30.imprint","IMPRINT",EDGE,{"disambiguationData":[TD([[subQ2,-1.0]])],"derivedFrom":subQ1}),1.0]])]});}
            var Q4;
            {var subQ0=sQuery(id+"F30.wireOp",EDGE,"E65.1");var subQ1=sQuery(id+"F30.wireOp",EDGE,"E64.bottom");var subQ2=makeQuery(id+"F30.imprint","INTERSECT",VERTEX,{"disambiguationData":[OD(0.0)],"derivedFrom":[subQ1,subQ0]});Q4=makeQuery(id+"F30.imprint","IMPRINT",FACE,{"disambiguationData":[TD([[makeQuery(id+"F30.imprint","IMPRINT",EDGE,{"disambiguationData":[TD([[subQ2,-1.0]])],"derivedFrom":subQ1}),-1.0]])]});}
            var Q5;
            {var subQ0=sQuery(id+"F30.wireOp",EDGE,"E65.1");var subQ1=sQuery(id+"F30.wireOp",EDGE,"E64.left");var subQ2=makeQuery(id+"F30.imprint","INTERSECT",VERTEX,{"disambiguationData":[OD(0.0)],"derivedFrom":[subQ1,subQ0]});Q5=makeQuery(id+"F30.imprint","IMPRINT",FACE,{"disambiguationData":[TD([[makeQuery(id+"F30.imprint","IMPRINT",EDGE,{"disambiguationData":[TD([[subQ2,-1.0]])],"derivedFrom":subQ1}),1.0]])]});}
            var Q6;
            {var subQ0=sQuery(id+"F30.wireOp",EDGE,"E65.1");var subQ1=sQuery(id+"F30.wireOp",EDGE,"E64.right");var subQ2=makeQuery(id+"F30.imprint","INTERSECT",VERTEX,{"disambiguationData":[OD(0.0)],"derivedFrom":[subQ1,subQ0]});Q6=makeQuery(id+"F30.imprint","IMPRINT",FACE,{"disambiguationData":[TD([[makeQuery(id+"F30.imprint","IMPRINT",EDGE,{"disambiguationData":[TD([[subQ2,-1.0]])],"derivedFrom":subQ1}),-1.0]])]});}
            var Q7;
            {var subQ0=sQuery(id+"F30.wireOp",EDGE,"E65.1");var subQ1=sQuery(id+"F30.wireOp",EDGE,"E64.top");var subQ2=makeQuery(id+"F30.imprint","INTERSECT",VERTEX,{"disambiguationData":[OD(0.0)],"derivedFrom":[subQ1,subQ0]});Q7=makeQuery(id+"F30.imprint","IMPRINT",FACE,{"disambiguationData":[TD([[makeQuery(id+"F30.imprint","IMPRINT",EDGE,{"disambiguationData":[TD([[subQ2,-1.0]])],"derivedFrom":subQ1}),1.0]])]});}
            extrude(context, id + "F31", {"entities" : qUnion([Q0, Q1, Q2, Q3, Q4, Q5, Q6, Q7]), "operationType" : NewBodyOperationType.ADD, "depth" : 3.86 * mm, "offsetDistance" : 25.4 * mm});
        }
        {
            var Q0;
            Q0=makeQuery(id+"F27.boolean.opBoolean","COPY",FACE,{"derivedFrom":makeQuery(id+"F27.opExtrude","CAP_FACE",FACE,{"disambiguationData":[OSD([sQuery(id+"F26.wireOp",EDGE,"E58.0")])],"isStart":false})});
            var sketch = newSketch(context, id + "F32", { "sketchPlane" : qUnion([Q0])});
            skLineSegment(sketch, "E66.0.0", {"start": v(-1.17, 9.14) * mm, "end": v(-3.48, 9.14) * mm});
            skArc(sketch, "E66.0.1", {"start": v(-3.48, 9.14) * mm, "mid": v(-2.33, 9.42) * mm, "end": v(-1.17, 9.14) * mm});
            skLineSegment(sketch, "E66.1.0", {"start": v(-4.58, 8.05) * mm, "end": v(-4.58, 5.74) * mm});
            skArc(sketch, "E66.1.1", {"start": v(-4.58, 5.74) * mm, "mid": v(-4.86, 6.9) * mm, "end": v(-4.58, 8.05) * mm});
            skLineSegment(sketch, "E66.2.0", {"start": v(-3.48, 4.65) * mm, "end": v(-1.17, 4.65) * mm});
            skArc(sketch, "E66.2.1", {"start": v(-1.17, 4.65) * mm, "mid": v(-2.33, 4.37) * mm, "end": v(-3.48, 4.65) * mm});
            skLineSegment(sketch, "E66.3.0", {"start": v(-0.08, 5.74) * mm, "end": v(-0.08, 8.05) * mm});
            skArc(sketch, "E66.3.1", {"start": v(-0.08, 8.05) * mm, "mid": v(0.2, 6.9) * mm, "end": v(-0.08, 5.74) * mm});
            skLineSegment(sketch, "E66.4.0", {"start": v(12.7, 9.14) * mm, "end": v(10.4, 9.14) * mm});
            skArc(sketch, "E66.4.1", {"start": v(10.4, 9.14) * mm, "mid": v(11.55, 9.42) * mm, "end": v(12.7, 9.14) * mm});
            skArc(sketch, "E66.5.0", {"start": v(9.3, 5.74) * mm, "mid": v(9.03, 6.9) * mm, "end": v(9.3, 8.05) * mm});
            skLineSegment(sketch, "E66.5.1", {"start": v(9.3, 8.05) * mm, "end": v(9.3, 5.74) * mm});
            skArc(sketch, "E66.6.0", {"start": v(12.7, 4.65) * mm, "mid": v(11.55, 4.37) * mm, "end": v(10.4, 4.65) * mm});
            skLineSegment(sketch, "E66.6.1", {"start": v(10.4, 4.65) * mm, "end": v(12.7, 4.65) * mm});
            skLineSegment(sketch, "E66.7.0", {"start": v(13.8, 5.74) * mm, "end": v(13.8, 8.05) * mm});
            skArc(sketch, "E66.7.1", {"start": v(13.8, 8.05) * mm, "mid": v(14.08, 6.9) * mm, "end": v(13.8, 5.74) * mm});
            skSolve(sketch);
        }
        {
            var Q0;
            Q0=qSketchRegion(id+"F32",true);
            extrude(context, id + "F33", {"entities" : qUnion([Q0]), "operationType" : NewBodyOperationType.ADD, "depth" : 3.86 * mm, "offsetDistance" : 25.4 * mm});
        }
        {
            var Q0;
            Q0=makeQuery(id+"F9.boolean.opBoolean","MERGE",FACE,{"derivedFrom":[makeQuery(id+"F1.opExtrude","CAP_FACE",FACE,{"disambiguationData":[OSD([sQuery(id+"F0.wireOp",EDGE,"E0.bottom"),sQuery(id+"F0.wireOp",EDGE,"E0.top"),sQuery(id+"F0.wireOp",EDGE,"E0.left"),sQuery(id+"F0.wireOp",EDGE,"E0.right")])],"isStart":false}),makeQuery(id+"F9.opExtrude","CAP_FACE",FACE,{"disambiguationData":[OSD([sQuery(id+"F8.wireOp",EDGE,"E8")])],"isStart":false})]});
            var sketch = newSketch(context, id + "F34", { "sketchPlane" : qUnion([Q0])});
            skLineSegment(sketch, "E67", {"start": v(-12.61, -18.5) * mm, "end": v(15.28, 9.27) * mm, "construction": true});
            skLineSegment(sketch, "E68", {"start": v(-5.58, -14.76) * mm, "end": v(-8.75, -11.58) * mm});
            skLineSegment(sketch, "E69", {"start": v(-8.75, -11.58) * mm, "end": v(-5.57, -8.4) * mm});
            skLineSegment(sketch, "E70", {"start": v(-5.57, -8.4) * mm, "end": v(-2.4, -11.6) * mm});
            skLineSegment(sketch, "E71", {"start": v(-2.4, -11.6) * mm, "end": v(-5.58, -14.76) * mm});
            skLineSegment(sketch, "E72", {"start": v(-7.16, -10) * mm, "end": v(-3.99, -13.18) * mm});
            skPoint(sketch, "E73", {"position": v(-5.57, -11.58) * mm});
            skLineSegment(sketch, "E74.1.0", {"start": v(11.49, -11.53) * mm, "end": v(8.3, -14.7) * mm});
            skLineSegment(sketch, "E74.1.1", {"start": v(8.31, -8.34) * mm, "end": v(11.49, -11.53) * mm});
            skLineSegment(sketch, "E74.1.2", {"start": v(5.13, -11.51) * mm, "end": v(8.31, -8.34) * mm});
            skLineSegment(sketch, "E74.1.3", {"start": v(8.3, -14.7) * mm, "end": v(5.13, -11.51) * mm});
            skLineSegment(sketch, "E74.2.0", {"start": v(8.25, 5.54) * mm, "end": v(11.42, 2.35) * mm});
            skLineSegment(sketch, "E74.2.1", {"start": v(5.06, 2.37) * mm, "end": v(8.25, 5.54) * mm});
            skLineSegment(sketch, "E74.2.2", {"start": v(8.24, -0.82) * mm, "end": v(5.06, 2.37) * mm});
            skLineSegment(sketch, "E74.2.3", {"start": v(11.42, 2.35) * mm, "end": v(8.24, -0.82) * mm});
            skLineSegment(sketch, "E74.3.0", {"start": v(-8.82, 2.3) * mm, "end": v(-5.63, 5.48) * mm});
            skLineSegment(sketch, "E74.3.1", {"start": v(-5.65, -0.88) * mm, "end": v(-8.82, 2.3) * mm});
            skLineSegment(sketch, "E74.3.2", {"start": v(-2.46, 2.29) * mm, "end": v(-5.65, -0.88) * mm});
            skLineSegment(sketch, "E74.3.3", {"start": v(-5.63, 5.48) * mm, "end": v(-2.46, 2.29) * mm});
            skPoint(sketch, "E74.center", {"position": v(1.33, -4.61) * mm});
            skCircle(sketch, "E75.0", {"center": v(-5.57, -11.58) * mm, "radius": 2.53 * mm});
            skCircle(sketch, "E76.1.0", {"center": v(8.3, -11.52) * mm, "radius": 2.53 * mm});
            skCircle(sketch, "E76.2.0", {"center": v(8.24, 2.36) * mm, "radius": 2.53 * mm});
            skCircle(sketch, "E76.3.0", {"center": v(-5.64, 2.3) * mm, "radius": 2.53 * mm});
            skSolve(sketch);
        }
        {
            var Q0;
            {var subQ0=sQuery(id+"F34.wireOp",EDGE,"E76.1.0");var subQ1=sQuery(id+"F34.wireOp",EDGE,"E74.1.0");var subQ2=makeQuery(id+"F34.imprint","INTERSECT",VERTEX,{"disambiguationData":[OD(0.0)],"derivedFrom":[subQ1,subQ0]});Q0=makeQuery(id+"F34.imprint","IMPRINT",FACE,{"disambiguationData":[TD([[makeQuery(id+"F34.imprint","IMPRINT",EDGE,{"disambiguationData":[TD([[subQ2,-1.0]])],"derivedFrom":subQ1}),1.0]])]});}
            var Q1;
            {var subQ0=sQuery(id+"F34.wireOp",EDGE,"E76.1.0");var subQ1=sQuery(id+"F34.wireOp",EDGE,"E74.1.3");var subQ2=makeQuery(id+"F34.imprint","INTERSECT",VERTEX,{"disambiguationData":[OD(0.0)],"derivedFrom":[subQ1,subQ0]});Q1=makeQuery(id+"F34.imprint","IMPRINT",FACE,{"disambiguationData":[TD([[makeQuery(id+"F34.imprint","IMPRINT",EDGE,{"disambiguationData":[TD([[subQ2,-1.0]])],"derivedFrom":subQ1}),1.0]])]});}
            var Q2;
            {var subQ0=sQuery(id+"F34.wireOp",EDGE,"E76.1.0");var subQ1=sQuery(id+"F34.wireOp",EDGE,"E74.1.1");var subQ2=makeQuery(id+"F34.imprint","INTERSECT",VERTEX,{"disambiguationData":[OD(0.0)],"derivedFrom":[subQ1,subQ0]});Q2=makeQuery(id+"F34.imprint","IMPRINT",FACE,{"disambiguationData":[TD([[makeQuery(id+"F34.imprint","IMPRINT",EDGE,{"disambiguationData":[TD([[subQ2,-1.0]])],"derivedFrom":subQ1}),1.0]])]});}
            var Q3;
            {var subQ0=sQuery(id+"F34.wireOp",EDGE,"E76.1.0");var subQ1=sQuery(id+"F34.wireOp",EDGE,"E74.1.2");var subQ2=makeQuery(id+"F34.imprint","INTERSECT",VERTEX,{"disambiguationData":[OD(0.0)],"derivedFrom":[subQ1,subQ0]});Q3=makeQuery(id+"F34.imprint","IMPRINT",FACE,{"disambiguationData":[TD([[makeQuery(id+"F34.imprint","IMPRINT",EDGE,{"disambiguationData":[TD([[subQ2,-1.0]])],"derivedFrom":subQ1}),1.0]])]});}
            var Q4;
            {var subQ0=sQuery(id+"F34.wireOp",EDGE,"E69");var subQ1=makeQuery(id+"F34.imprint","INTERSECT",VERTEX,{"derivedFrom":[subQ0,sQuery(id+"F34.wireOp",EDGE,"E72")]});Q4=makeQuery(id+"F34.imprint","IMPRINT",FACE,{"disambiguationData":[TD([[makeQuery(id+"F34.imprint","IMPRINT",EDGE,{"disambiguationData":[TD([[subQ1,1.0]])],"derivedFrom":subQ0}),1.0]])]});}
            var Q5;
            {var subQ0=sQuery(id+"F34.wireOp",EDGE,"E75.0");var subQ1=sQuery(id+"F34.wireOp",EDGE,"E70");var subQ2=makeQuery(id+"F34.imprint","INTERSECT",VERTEX,{"disambiguationData":[OD(0.0)],"derivedFrom":[subQ1,subQ0]});Q5=makeQuery(id+"F34.imprint","IMPRINT",FACE,{"disambiguationData":[TD([[makeQuery(id+"F34.imprint","IMPRINT",EDGE,{"disambiguationData":[TD([[subQ2,-1.0]])],"derivedFrom":subQ1}),1.0]])]});}
            var Q6;
            {var subQ0=sQuery(id+"F34.wireOp",EDGE,"E71");var subQ1=makeQuery(id+"F34.imprint","INTERSECT",VERTEX,{"derivedFrom":[subQ0,sQuery(id+"F34.wireOp",EDGE,"E72")]});Q6=makeQuery(id+"F34.imprint","IMPRINT",FACE,{"disambiguationData":[TD([[makeQuery(id+"F34.imprint","IMPRINT",EDGE,{"disambiguationData":[TD([[subQ1,1.0]])],"derivedFrom":subQ0}),1.0]])]});}
            var Q7;
            {var subQ0=sQuery(id+"F34.wireOp",EDGE,"E75.0");var subQ1=sQuery(id+"F34.wireOp",EDGE,"E68");var subQ2=makeQuery(id+"F34.imprint","INTERSECT",VERTEX,{"disambiguationData":[OD(0.0)],"derivedFrom":[subQ1,subQ0]});Q7=makeQuery(id+"F34.imprint","IMPRINT",FACE,{"disambiguationData":[TD([[makeQuery(id+"F34.imprint","IMPRINT",EDGE,{"disambiguationData":[TD([[subQ2,-1.0]])],"derivedFrom":subQ1}),1.0]])]});}
            var Q8;
            {var subQ0=sQuery(id+"F34.wireOp",EDGE,"E76.3.0");var subQ1=sQuery(id+"F34.wireOp",EDGE,"E74.3.0");var subQ2=makeQuery(id+"F34.imprint","INTERSECT",VERTEX,{"disambiguationData":[OD(0.0)],"derivedFrom":[subQ1,subQ0]});Q8=makeQuery(id+"F34.imprint","IMPRINT",FACE,{"disambiguationData":[TD([[makeQuery(id+"F34.imprint","IMPRINT",EDGE,{"disambiguationData":[TD([[subQ2,-1.0]])],"derivedFrom":subQ1}),1.0]])]});}
            var Q9;
            {var subQ0=sQuery(id+"F34.wireOp",EDGE,"E76.3.0");var subQ1=sQuery(id+"F34.wireOp",EDGE,"E74.3.3");var subQ2=makeQuery(id+"F34.imprint","INTERSECT",VERTEX,{"disambiguationData":[OD(0.0)],"derivedFrom":[subQ1,subQ0]});Q9=makeQuery(id+"F34.imprint","IMPRINT",FACE,{"disambiguationData":[TD([[makeQuery(id+"F34.imprint","IMPRINT",EDGE,{"disambiguationData":[TD([[subQ2,-1.0]])],"derivedFrom":subQ1}),1.0]])]});}
            var Q10;
            {var subQ0=sQuery(id+"F34.wireOp",EDGE,"E76.3.0");var subQ1=sQuery(id+"F34.wireOp",EDGE,"E74.3.1");var subQ2=makeQuery(id+"F34.imprint","INTERSECT",VERTEX,{"disambiguationData":[OD(0.0)],"derivedFrom":[subQ1,subQ0]});Q10=makeQuery(id+"F34.imprint","IMPRINT",FACE,{"disambiguationData":[TD([[makeQuery(id+"F34.imprint","IMPRINT",EDGE,{"disambiguationData":[TD([[subQ2,-1.0]])],"derivedFrom":subQ1}),1.0]])]});}
            var Q11;
            {var subQ0=sQuery(id+"F34.wireOp",EDGE,"E76.3.0");var subQ1=sQuery(id+"F34.wireOp",EDGE,"E74.3.2");var subQ2=makeQuery(id+"F34.imprint","INTERSECT",VERTEX,{"disambiguationData":[OD(0.0)],"derivedFrom":[subQ1,subQ0]});Q11=makeQuery(id+"F34.imprint","IMPRINT",FACE,{"disambiguationData":[TD([[makeQuery(id+"F34.imprint","IMPRINT",EDGE,{"disambiguationData":[TD([[subQ2,-1.0]])],"derivedFrom":subQ1}),1.0]])]});}
            var Q12;
            {var subQ0=sQuery(id+"F34.wireOp",EDGE,"E76.2.0");var subQ1=sQuery(id+"F34.wireOp",EDGE,"E74.2.0");var subQ2=makeQuery(id+"F34.imprint","INTERSECT",VERTEX,{"disambiguationData":[OD(0.0)],"derivedFrom":[subQ1,subQ0]});Q12=makeQuery(id+"F34.imprint","IMPRINT",FACE,{"disambiguationData":[TD([[makeQuery(id+"F34.imprint","IMPRINT",EDGE,{"disambiguationData":[TD([[subQ2,-1.0]])],"derivedFrom":subQ1}),1.0]])]});}
            var Q13;
            {var subQ0=sQuery(id+"F34.wireOp",EDGE,"E76.2.0");var subQ1=sQuery(id+"F34.wireOp",EDGE,"E74.2.1");var subQ2=makeQuery(id+"F34.imprint","INTERSECT",VERTEX,{"disambiguationData":[OD(0.0)],"derivedFrom":[subQ1,subQ0]});Q13=makeQuery(id+"F34.imprint","IMPRINT",FACE,{"disambiguationData":[TD([[makeQuery(id+"F34.imprint","IMPRINT",EDGE,{"disambiguationData":[TD([[subQ2,-1.0]])],"derivedFrom":subQ1}),1.0]])]});}
            var Q14;
            {var subQ0=sQuery(id+"F34.wireOp",EDGE,"E76.2.0");var subQ1=sQuery(id+"F34.wireOp",EDGE,"E74.2.2");var subQ2=makeQuery(id+"F34.imprint","INTERSECT",VERTEX,{"disambiguationData":[OD(0.0)],"derivedFrom":[subQ1,subQ0]});Q14=makeQuery(id+"F34.imprint","IMPRINT",FACE,{"disambiguationData":[TD([[makeQuery(id+"F34.imprint","IMPRINT",EDGE,{"disambiguationData":[TD([[subQ2,-1.0]])],"derivedFrom":subQ1}),1.0]])]});}
            var Q15;
            {var subQ0=sQuery(id+"F34.wireOp",EDGE,"E76.2.0");var subQ1=sQuery(id+"F34.wireOp",EDGE,"E74.2.3");var subQ2=makeQuery(id+"F34.imprint","INTERSECT",VERTEX,{"disambiguationData":[OD(0.0)],"derivedFrom":[subQ1,subQ0]});Q15=makeQuery(id+"F34.imprint","IMPRINT",FACE,{"disambiguationData":[TD([[makeQuery(id+"F34.imprint","IMPRINT",EDGE,{"disambiguationData":[TD([[subQ2,-1.0]])],"derivedFrom":subQ1}),1.0]])]});}
            extrude(context, id + "F35", {"entities" : qUnion([Q0, Q1, Q2, Q3, Q4, Q5, Q6, Q7, Q8, Q9, Q10, Q11, Q12, Q13, Q14, Q15]), "operationType" : NewBodyOperationType.ADD, "oppositeDirection" : true, "depth" : 13.8 * mm, "offsetDistance" : 25.4 * mm});
        }
        {
            var Q0;
            {var subQ0=sQuery(id+"F34.wireOp",EDGE,"E76.3.0");var subQ1=sQuery(id+"F34.wireOp",EDGE,"E76.2.0");var subQ2=sQuery(id+"F34.wireOp",EDGE,"E76.1.0");var subQ3=sQuery(id+"F34.wireOp",EDGE,"E75.0");Q0=makeQuery(id+"F35.boolean.opBoolean","MERGE",FACE,{"derivedFrom":[makeQuery(id+"F9.boolean.opBoolean","MERGE",FACE,{"derivedFrom":[makeQuery(id+"F1.opExtrude","CAP_FACE",FACE,{"disambiguationData":[OSD([sQuery(id+"F0.wireOp",EDGE,"E0.bottom"),sQuery(id+"F0.wireOp",EDGE,"E0.top"),sQuery(id+"F0.wireOp",EDGE,"E0.left"),sQuery(id+"F0.wireOp",EDGE,"E0.right")])],"isStart":false}),makeQuery(id+"F9.opExtrude","CAP_FACE",FACE,{"disambiguationData":[OSD([sQuery(id+"F8.wireOp",EDGE,"E8")])],"isStart":false})]}),makeQuery(id+"F35.opExtrude","CAP_FACE",FACE,{"disambiguationData":[OSD([sQuery(id+"F34.wireOp",EDGE,"E68"),subQ3])],"isStart":true}),makeQuery(id+"F35.opExtrude","CAP_FACE",FACE,{"disambiguationData":[OSD([sQuery(id+"F34.wireOp",EDGE,"E69"),subQ3])],"isStart":true}),makeQuery(id+"F35.opExtrude","CAP_FACE",FACE,{"disambiguationData":[OSD([sQuery(id+"F34.wireOp",EDGE,"E70"),subQ3])],"isStart":true}),makeQuery(id+"F35.opExtrude","CAP_FACE",FACE,{"disambiguationData":[OSD([sQuery(id+"F34.wireOp",EDGE,"E71"),subQ3])],"isStart":true}),makeQuery(id+"F35.opExtrude","CAP_FACE",FACE,{"disambiguationData":[OSD([sQuery(id+"F34.wireOp",EDGE,"E74.1.0"),subQ2])],"isStart":true}),makeQuery(id+"F35.opExtrude","CAP_FACE",FACE,{"disambiguationData":[OSD([sQuery(id+"F34.wireOp",EDGE,"E74.1.1"),subQ2])],"isStart":true}),makeQuery(id+"F35.opExtrude","CAP_FACE",FACE,{"disambiguationData":[OSD([sQuery(id+"F34.wireOp",EDGE,"E74.1.2"),subQ2])],"isStart":true}),makeQuery(id+"F35.opExtrude","CAP_FACE",FACE,{"disambiguationData":[OSD([sQuery(id+"F34.wireOp",EDGE,"E74.1.3"),subQ2])],"isStart":true}),makeQuery(id+"F35.opExtrude","CAP_FACE",FACE,{"disambiguationData":[OSD([sQuery(id+"F34.wireOp",EDGE,"E74.2.0"),subQ1])],"isStart":true}),makeQuery(id+"F35.opExtrude","CAP_FACE",FACE,{"disambiguationData":[OSD([sQuery(id+"F34.wireOp",EDGE,"E74.2.1"),subQ1])],"isStart":true}),makeQuery(id+"F35.opExtrude","CAP_FACE",FACE,{"disambiguationData":[OSD([sQuery(id+"F34.wireOp",EDGE,"E74.2.2"),subQ1])],"isStart":true}),makeQuery(id+"F35.opExtrude","CAP_FACE",FACE,{"disambiguationData":[OSD([sQuery(id+"F34.wireOp",EDGE,"E74.2.3"),subQ1])],"isStart":true}),makeQuery(id+"F35.opExtrude","CAP_FACE",FACE,{"disambiguationData":[OSD([sQuery(id+"F34.wireOp",EDGE,"E74.3.0"),subQ0])],"isStart":true}),makeQuery(id+"F35.opExtrude","CAP_FACE",FACE,{"disambiguationData":[OSD([sQuery(id+"F34.wireOp",EDGE,"E74.3.1"),subQ0])],"isStart":true}),makeQuery(id+"F35.opExtrude","CAP_FACE",FACE,{"disambiguationData":[OSD([sQuery(id+"F34.wireOp",EDGE,"E74.3.2"),subQ0])],"isStart":true}),makeQuery(id+"F35.opExtrude","CAP_FACE",FACE,{"disambiguationData":[OSD([sQuery(id+"F34.wireOp",EDGE,"E74.3.3"),subQ0])],"isStart":true})]});}
            var sketch = newSketch(context, id + "F36", { "sketchPlane" : qUnion([Q0])});
            skCircle(sketch, "E77", {"center": v(8.24, 2.36) * mm, "radius": 2.53 * mm});
            skLineSegment(sketch, "E78.0", {"start": v(10.65, 1.58) * mm, "end": v(9.01, -0.05) * mm});
            skLineSegment(sketch, "E78.1", {"start": v(9.02, 4.76) * mm, "end": v(10.65, 3.13) * mm});
            skLineSegment(sketch, "E78.2", {"start": v(5.84, 3.14) * mm, "end": v(7.48, 4.77) * mm});
            skLineSegment(sketch, "E78.3", {"start": v(7.46, -0.04) * mm, "end": v(5.84, 1.6) * mm});
            skCircle(sketch, "E79.1.0", {"center": v(-5.64, 2.3) * mm, "radius": 2.53 * mm});
            skLineSegment(sketch, "E79.1.1", {"start": v(-4.86, 4.7) * mm, "end": v(-3.23, 3.06) * mm});
            skLineSegment(sketch, "E79.1.2", {"start": v(-8.04, 3.07) * mm, "end": v(-6.4, 4.7) * mm});
            skLineSegment(sketch, "E79.1.3", {"start": v(-6.42, -0.1) * mm, "end": v(-8.05, 1.53) * mm});
            skLineSegment(sketch, "E79.1.4", {"start": v(-3.23, 1.52) * mm, "end": v(-4.87, -0.11) * mm});
            skCircle(sketch, "E79.2.0", {"center": v(-5.57, -11.58) * mm, "radius": 2.53 * mm});
            skLineSegment(sketch, "E79.2.1", {"start": v(-7.98, -10.8) * mm, "end": v(-6.34, -9.18) * mm});
            skLineSegment(sketch, "E79.2.2", {"start": v(-6.35, -13.99) * mm, "end": v(-7.98, -12.35) * mm});
            skLineSegment(sketch, "E79.2.3", {"start": v(-3.17, -12.36) * mm, "end": v(-4.8, -14) * mm});
            skLineSegment(sketch, "E79.2.4", {"start": v(-4.8, -9.18) * mm, "end": v(-3.17, -10.82) * mm});
            skCircle(sketch, "E79.3.0", {"center": v(8.3, -11.52) * mm, "radius": 2.53 * mm});
            skLineSegment(sketch, "E79.3.1", {"start": v(7.53, -13.93) * mm, "end": v(5.9, -12.29) * mm});
            skLineSegment(sketch, "E79.3.2", {"start": v(10.71, -12.3) * mm, "end": v(9.07, -13.93) * mm});
            skLineSegment(sketch, "E79.3.3", {"start": v(9.08, -9.12) * mm, "end": v(10.71, -10.75) * mm});
            skLineSegment(sketch, "E79.3.4", {"start": v(5.9, -10.74) * mm, "end": v(7.54, -9.11) * mm});
            skPoint(sketch, "E79.center", {"position": v(1.33, -4.61) * mm});
            skSolve(sketch);
        }
        {
            var Q0;
            {var subQ0=sQuery(id+"F36.wireOp",EDGE,"E78.1");var subQ1=sQuery(id+"F36.wireOp",EDGE,"E77");var subQ2=makeQuery(id+"F36.imprint","INTERSECT",VERTEX,{"disambiguationData":[OD(0.0)],"derivedFrom":[subQ1,subQ0]});Q0=makeQuery(id+"F36.imprint","IMPRINT",FACE,{"disambiguationData":[TD([[makeQuery(id+"F36.imprint","IMPRINT",EDGE,{"disambiguationData":[TD([[subQ2,1.0]])],"derivedFrom":subQ1}),1.0]])]});}
            var Q1;
            {var subQ0=sQuery(id+"F36.wireOp",EDGE,"E78.2");var subQ1=sQuery(id+"F36.wireOp",EDGE,"E77");var subQ2=makeQuery(id+"F36.imprint","INTERSECT",VERTEX,{"disambiguationData":[OD(0.0)],"derivedFrom":[subQ1,subQ0]});Q1=makeQuery(id+"F36.imprint","IMPRINT",FACE,{"disambiguationData":[TD([[makeQuery(id+"F36.imprint","IMPRINT",EDGE,{"disambiguationData":[TD([[subQ2,-1.0]])],"derivedFrom":subQ1}),1.0]])]});}
            var Q2;
            {var subQ0=sQuery(id+"F36.wireOp",EDGE,"E78.3");var subQ1=sQuery(id+"F36.wireOp",EDGE,"E77");var subQ2=makeQuery(id+"F36.imprint","INTERSECT",VERTEX,{"disambiguationData":[OD(0.0)],"derivedFrom":[subQ1,subQ0]});Q2=makeQuery(id+"F36.imprint","IMPRINT",FACE,{"disambiguationData":[TD([[makeQuery(id+"F36.imprint","IMPRINT",EDGE,{"disambiguationData":[TD([[subQ2,-1.0]])],"derivedFrom":subQ1}),1.0]])]});}
            var Q3;
            {var subQ0=sQuery(id+"F36.wireOp",EDGE,"E78.0");var subQ1=sQuery(id+"F36.wireOp",EDGE,"E77");var subQ2=makeQuery(id+"F36.imprint","INTERSECT",VERTEX,{"disambiguationData":[OD(0.0)],"derivedFrom":[subQ1,subQ0]});Q3=makeQuery(id+"F36.imprint","IMPRINT",FACE,{"disambiguationData":[TD([[makeQuery(id+"F36.imprint","IMPRINT",EDGE,{"disambiguationData":[TD([[subQ2,-1.0]])],"derivedFrom":subQ1}),1.0]])]});}
            var Q4;
            {var subQ0=sQuery(id+"F36.wireOp",EDGE,"E79.1.2");var subQ1=sQuery(id+"F36.wireOp",EDGE,"E79.1.0");var subQ2=makeQuery(id+"F36.imprint","INTERSECT",VERTEX,{"disambiguationData":[OD(0.0)],"derivedFrom":[subQ1,subQ0]});Q4=makeQuery(id+"F36.imprint","IMPRINT",FACE,{"disambiguationData":[TD([[makeQuery(id+"F36.imprint","IMPRINT",EDGE,{"disambiguationData":[TD([[subQ2,1.0]])],"derivedFrom":subQ1}),1.0]])]});}
            var Q5;
            {var subQ0=sQuery(id+"F36.wireOp",EDGE,"E79.1.3");var subQ1=sQuery(id+"F36.wireOp",EDGE,"E79.1.0");var subQ2=makeQuery(id+"F36.imprint","INTERSECT",VERTEX,{"disambiguationData":[OD(0.0)],"derivedFrom":[subQ1,subQ0]});Q5=makeQuery(id+"F36.imprint","IMPRINT",FACE,{"disambiguationData":[TD([[makeQuery(id+"F36.imprint","IMPRINT",EDGE,{"disambiguationData":[TD([[subQ2,-1.0]])],"derivedFrom":subQ1}),1.0]])]});}
            var Q6;
            {var subQ0=sQuery(id+"F36.wireOp",EDGE,"E79.1.4");var subQ1=sQuery(id+"F36.wireOp",EDGE,"E79.1.0");var subQ2=makeQuery(id+"F36.imprint","INTERSECT",VERTEX,{"disambiguationData":[OD(0.0)],"derivedFrom":[subQ1,subQ0]});Q6=makeQuery(id+"F36.imprint","IMPRINT",FACE,{"disambiguationData":[TD([[makeQuery(id+"F36.imprint","IMPRINT",EDGE,{"disambiguationData":[TD([[subQ2,-1.0]])],"derivedFrom":subQ1}),1.0]])]});}
            var Q7;
            {var subQ0=sQuery(id+"F36.wireOp",EDGE,"E79.1.1");var subQ1=sQuery(id+"F36.wireOp",EDGE,"E79.1.0");var subQ2=makeQuery(id+"F36.imprint","INTERSECT",VERTEX,{"disambiguationData":[OD(0.0)],"derivedFrom":[subQ1,subQ0]});Q7=makeQuery(id+"F36.imprint","IMPRINT",FACE,{"disambiguationData":[TD([[makeQuery(id+"F36.imprint","IMPRINT",EDGE,{"disambiguationData":[TD([[subQ2,-1.0]])],"derivedFrom":subQ1}),1.0]])]});}
            var Q8;
            {var subQ0=sQuery(id+"F36.wireOp",EDGE,"E79.2.2");var subQ1=sQuery(id+"F36.wireOp",EDGE,"E79.2.0");var subQ2=makeQuery(id+"F36.imprint","INTERSECT",VERTEX,{"disambiguationData":[OD(0.0)],"derivedFrom":[subQ1,subQ0]});Q8=makeQuery(id+"F36.imprint","IMPRINT",FACE,{"disambiguationData":[TD([[makeQuery(id+"F36.imprint","IMPRINT",EDGE,{"disambiguationData":[TD([[subQ2,1.0]])],"derivedFrom":subQ1}),1.0]])]});}
            var Q9;
            {var subQ0=sQuery(id+"F36.wireOp",EDGE,"E79.2.3");var subQ1=sQuery(id+"F36.wireOp",EDGE,"E79.2.0");var subQ2=makeQuery(id+"F36.imprint","INTERSECT",VERTEX,{"disambiguationData":[OD(0.0)],"derivedFrom":[subQ1,subQ0]});Q9=makeQuery(id+"F36.imprint","IMPRINT",FACE,{"disambiguationData":[TD([[makeQuery(id+"F36.imprint","IMPRINT",EDGE,{"disambiguationData":[TD([[subQ2,-1.0]])],"derivedFrom":subQ1}),1.0]])]});}
            var Q10;
            {var subQ0=sQuery(id+"F36.wireOp",EDGE,"E79.2.4");var subQ1=sQuery(id+"F36.wireOp",EDGE,"E79.2.0");var subQ2=makeQuery(id+"F36.imprint","INTERSECT",VERTEX,{"disambiguationData":[OD(0.0)],"derivedFrom":[subQ1,subQ0]});Q10=makeQuery(id+"F36.imprint","IMPRINT",FACE,{"disambiguationData":[TD([[makeQuery(id+"F36.imprint","IMPRINT",EDGE,{"disambiguationData":[TD([[subQ2,-1.0]])],"derivedFrom":subQ1}),1.0]])]});}
            var Q11;
            {var subQ0=sQuery(id+"F36.wireOp",EDGE,"E79.2.1");var subQ1=sQuery(id+"F36.wireOp",EDGE,"E79.2.0");var subQ2=makeQuery(id+"F36.imprint","INTERSECT",VERTEX,{"disambiguationData":[OD(0.0)],"derivedFrom":[subQ1,subQ0]});Q11=makeQuery(id+"F36.imprint","IMPRINT",FACE,{"disambiguationData":[TD([[makeQuery(id+"F36.imprint","IMPRINT",EDGE,{"disambiguationData":[TD([[subQ2,-1.0]])],"derivedFrom":subQ1}),1.0]])]});}
            var Q12;
            {var subQ0=sQuery(id+"F36.wireOp",EDGE,"E79.3.2");var subQ1=sQuery(id+"F36.wireOp",EDGE,"E79.3.0");var subQ2=makeQuery(id+"F36.imprint","INTERSECT",VERTEX,{"disambiguationData":[OD(0.0)],"derivedFrom":[subQ1,subQ0]});Q12=makeQuery(id+"F36.imprint","IMPRINT",FACE,{"disambiguationData":[TD([[makeQuery(id+"F36.imprint","IMPRINT",EDGE,{"disambiguationData":[TD([[subQ2,1.0]])],"derivedFrom":subQ1}),1.0]])]});}
            var Q13;
            {var subQ0=sQuery(id+"F36.wireOp",EDGE,"E79.3.3");var subQ1=sQuery(id+"F36.wireOp",EDGE,"E79.3.0");var subQ2=makeQuery(id+"F36.imprint","INTERSECT",VERTEX,{"disambiguationData":[OD(0.0)],"derivedFrom":[subQ1,subQ0]});Q13=makeQuery(id+"F36.imprint","IMPRINT",FACE,{"disambiguationData":[TD([[makeQuery(id+"F36.imprint","IMPRINT",EDGE,{"disambiguationData":[TD([[subQ2,-1.0]])],"derivedFrom":subQ1}),1.0]])]});}
            var Q14;
            {var subQ0=sQuery(id+"F36.wireOp",EDGE,"E79.3.4");var subQ1=sQuery(id+"F36.wireOp",EDGE,"E79.3.0");var subQ2=makeQuery(id+"F36.imprint","INTERSECT",VERTEX,{"disambiguationData":[OD(0.0)],"derivedFrom":[subQ1,subQ0]});Q14=makeQuery(id+"F36.imprint","IMPRINT",FACE,{"disambiguationData":[TD([[makeQuery(id+"F36.imprint","IMPRINT",EDGE,{"disambiguationData":[TD([[subQ2,-1.0]])],"derivedFrom":subQ1}),1.0]])]});}
            var Q15;
            {var subQ0=sQuery(id+"F36.wireOp",EDGE,"E79.3.1");var subQ1=sQuery(id+"F36.wireOp",EDGE,"E79.3.0");var subQ2=makeQuery(id+"F36.imprint","INTERSECT",VERTEX,{"disambiguationData":[OD(0.0)],"derivedFrom":[subQ1,subQ0]});Q15=makeQuery(id+"F36.imprint","IMPRINT",FACE,{"disambiguationData":[TD([[makeQuery(id+"F36.imprint","IMPRINT",EDGE,{"disambiguationData":[TD([[subQ2,-1.0]])],"derivedFrom":subQ1}),1.0]])]});}
            extrude(context, id + "F37", {"entities" : qUnion([Q0, Q1, Q2, Q3, Q4, Q5, Q6, Q7, Q8, Q9, Q10, Q11, Q12, Q13, Q14, Q15]), "operationType" : NewBodyOperationType.REMOVE, "oppositeDirection" : true, "depth" : 0.38 * mm, "offsetDistance" : 25.4 * mm});
        }
        {
            var Q0;
            {var subQ0=sQuery(id+"F34.wireOp",EDGE,"E76.3.0");var subQ1=sQuery(id+"F34.wireOp",EDGE,"E76.2.0");var subQ2=sQuery(id+"F34.wireOp",EDGE,"E76.1.0");var subQ3=sQuery(id+"F34.wireOp",EDGE,"E75.0");Q0=makeQuery(id+"F35.boolean.opBoolean","MERGE",FACE,{"derivedFrom":[makeQuery(id+"F7.boolean.opBoolean","MERGE",FACE,{"derivedFrom":[makeQuery(id+"F1.opExtrude","CAP_FACE",FACE,{"disambiguationData":[OSD([sQuery(id+"F0.wireOp",EDGE,"E0.bottom"),sQuery(id+"F0.wireOp",EDGE,"E0.top"),sQuery(id+"F0.wireOp",EDGE,"E0.left"),sQuery(id+"F0.wireOp",EDGE,"E0.right")])],"isStart":true}),makeQuery(id+"F7.opExtrude","CAP_FACE",FACE,{"disambiguationData":[OSD([sQuery(id+"F6.wireOp",EDGE,"E5")])],"isStart":false})]}),makeQuery(id+"F35.opExtrude","CAP_FACE",FACE,{"disambiguationData":[OSD([sQuery(id+"F34.wireOp",EDGE,"E68"),subQ3])],"isStart":false}),makeQuery(id+"F35.opExtrude","CAP_FACE",FACE,{"disambiguationData":[OSD([sQuery(id+"F34.wireOp",EDGE,"E69"),subQ3])],"isStart":false}),makeQuery(id+"F35.opExtrude","CAP_FACE",FACE,{"disambiguationData":[OSD([sQuery(id+"F34.wireOp",EDGE,"E70"),subQ3])],"isStart":false}),makeQuery(id+"F35.opExtrude","CAP_FACE",FACE,{"disambiguationData":[OSD([sQuery(id+"F34.wireOp",EDGE,"E71"),subQ3])],"isStart":false}),makeQuery(id+"F35.opExtrude","CAP_FACE",FACE,{"disambiguationData":[OSD([sQuery(id+"F34.wireOp",EDGE,"E74.1.0"),subQ2])],"isStart":false}),makeQuery(id+"F35.opExtrude","CAP_FACE",FACE,{"disambiguationData":[OSD([sQuery(id+"F34.wireOp",EDGE,"E74.1.1"),subQ2])],"isStart":false}),makeQuery(id+"F35.opExtrude","CAP_FACE",FACE,{"disambiguationData":[OSD([sQuery(id+"F34.wireOp",EDGE,"E74.1.2"),subQ2])],"isStart":false}),makeQuery(id+"F35.opExtrude","CAP_FACE",FACE,{"disambiguationData":[OSD([sQuery(id+"F34.wireOp",EDGE,"E74.1.3"),subQ2])],"isStart":false}),makeQuery(id+"F35.opExtrude","CAP_FACE",FACE,{"disambiguationData":[OSD([sQuery(id+"F34.wireOp",EDGE,"E74.2.0"),subQ1])],"isStart":false}),makeQuery(id+"F35.opExtrude","CAP_FACE",FACE,{"disambiguationData":[OSD([sQuery(id+"F34.wireOp",EDGE,"E74.2.1"),subQ1])],"isStart":false}),makeQuery(id+"F35.opExtrude","CAP_FACE",FACE,{"disambiguationData":[OSD([sQuery(id+"F34.wireOp",EDGE,"E74.2.2"),subQ1])],"isStart":false}),makeQuery(id+"F35.opExtrude","CAP_FACE",FACE,{"disambiguationData":[OSD([sQuery(id+"F34.wireOp",EDGE,"E74.2.3"),subQ1])],"isStart":false}),makeQuery(id+"F35.opExtrude","CAP_FACE",FACE,{"disambiguationData":[OSD([sQuery(id+"F34.wireOp",EDGE,"E74.3.0"),subQ0])],"isStart":false}),makeQuery(id+"F35.opExtrude","CAP_FACE",FACE,{"disambiguationData":[OSD([sQuery(id+"F34.wireOp",EDGE,"E74.3.1"),subQ0])],"isStart":false}),makeQuery(id+"F35.opExtrude","CAP_FACE",FACE,{"disambiguationData":[OSD([sQuery(id+"F34.wireOp",EDGE,"E74.3.2"),subQ0])],"isStart":false}),makeQuery(id+"F35.opExtrude","CAP_FACE",FACE,{"disambiguationData":[OSD([sQuery(id+"F34.wireOp",EDGE,"E74.3.3"),subQ0])],"isStart":false})]});}
            var sketch = newSketch(context, id + "F38", { "sketchPlane" : qUnion([Q0])});
            skCircle(sketch, "E80", {"center": v(8.24, -2.36) * mm, "radius": 2.53 * mm});
            skLineSegment(sketch, "E81.0", {"start": v(5.84, -3.14) * mm, "end": v(7.48, -4.77) * mm});
            skLineSegment(sketch, "E81.1", {"start": v(9.02, -4.76) * mm, "end": v(10.65, -3.13) * mm});
            skLineSegment(sketch, "E81.3", {"start": v(10.65, -1.58) * mm, "end": v(9.01, 0.05) * mm});
            skLineSegment(sketch, "E81.4", {"start": v(7.46, 0.04) * mm, "end": v(5.84, -1.6) * mm});
            skCircle(sketch, "E82.1.0", {"center": v(8.3, 11.52) * mm, "radius": 2.53 * mm});
            skLineSegment(sketch, "E82.1.1", {"start": v(5.9, 10.74) * mm, "end": v(7.54, 9.11) * mm});
            skLineSegment(sketch, "E82.1.2", {"start": v(9.08, 9.12) * mm, "end": v(10.71, 10.75) * mm});
            skLineSegment(sketch, "E82.1.3", {"start": v(10.71, 12.3) * mm, "end": v(9.07, 13.93) * mm});
            skLineSegment(sketch, "E82.1.4", {"start": v(7.53, 13.93) * mm, "end": v(5.9, 12.29) * mm});
            skCircle(sketch, "E82.2.0", {"center": v(-5.57, 11.58) * mm, "radius": 2.53 * mm});
            skLineSegment(sketch, "E82.2.1", {"start": v(-4.8, 9.18) * mm, "end": v(-3.17, 10.82) * mm});
            skLineSegment(sketch, "E82.2.2", {"start": v(-3.17, 12.36) * mm, "end": v(-4.8, 14) * mm});
            skLineSegment(sketch, "E82.2.3", {"start": v(-6.35, 13.99) * mm, "end": v(-7.98, 12.35) * mm});
            skLineSegment(sketch, "E82.2.4", {"start": v(-7.98, 10.8) * mm, "end": v(-6.34, 9.18) * mm});
            skCircle(sketch, "E82.3.0", {"center": v(-5.64, -2.3) * mm, "radius": 2.53 * mm});
            skLineSegment(sketch, "E82.3.1", {"start": v(-3.23, -1.52) * mm, "end": v(-4.87, 0.11) * mm});
            skLineSegment(sketch, "E82.3.2", {"start": v(-6.42, 0.1) * mm, "end": v(-8.05, -1.53) * mm});
            skLineSegment(sketch, "E82.3.3", {"start": v(-8.04, -3.07) * mm, "end": v(-6.4, -4.7) * mm});
            skLineSegment(sketch, "E82.3.4", {"start": v(-4.86, -4.7) * mm, "end": v(-3.23, -3.06) * mm});
            skPoint(sketch, "E82.center", {"position": v(1.33, 4.61) * mm});
            skSolve(sketch);
        }
        {
            var Q0;
            {var subQ0=sQuery(id+"F38.wireOp",EDGE,"E81.3");Q0=makeQuery(id+"F38.imprint","IMPRINT",FACE,{"disambiguationData":[TD([[makeQuery(id+"F38.imprint","IMPRINT",EDGE,{"derivedFrom":subQ0}),-1.0]])]});}
            var Q1;
            {var subQ0=sQuery(id+"F38.wireOp",EDGE,"E81.4");Q1=makeQuery(id+"F38.imprint","IMPRINT",FACE,{"disambiguationData":[TD([[makeQuery(id+"F38.imprint","IMPRINT",EDGE,{"derivedFrom":subQ0}),-1.0]])]});}
            var Q2;
            {var subQ0=sQuery(id+"F38.wireOp",EDGE,"E81.0");Q2=makeQuery(id+"F38.imprint","IMPRINT",FACE,{"disambiguationData":[TD([[makeQuery(id+"F38.imprint","IMPRINT",EDGE,{"derivedFrom":subQ0}),-1.0]])]});}
            var Q3;
            {var subQ0=sQuery(id+"F38.wireOp",EDGE,"E81.1");Q3=makeQuery(id+"F38.imprint","IMPRINT",FACE,{"disambiguationData":[TD([[makeQuery(id+"F38.imprint","IMPRINT",EDGE,{"derivedFrom":subQ0}),-1.0]])]});}
            var Q4;
            {var subQ0=sQuery(id+"F38.wireOp",EDGE,"E82.1.4");Q4=makeQuery(id+"F38.imprint","IMPRINT",FACE,{"disambiguationData":[TD([[makeQuery(id+"F38.imprint","IMPRINT",EDGE,{"derivedFrom":subQ0}),-1.0]])]});}
            var Q5;
            {var subQ0=sQuery(id+"F38.wireOp",EDGE,"E82.1.1");Q5=makeQuery(id+"F38.imprint","IMPRINT",FACE,{"disambiguationData":[TD([[makeQuery(id+"F38.imprint","IMPRINT",EDGE,{"derivedFrom":subQ0}),-1.0]])]});}
            var Q6;
            {var subQ0=sQuery(id+"F38.wireOp",EDGE,"E82.1.2");Q6=makeQuery(id+"F38.imprint","IMPRINT",FACE,{"disambiguationData":[TD([[makeQuery(id+"F38.imprint","IMPRINT",EDGE,{"derivedFrom":subQ0}),-1.0]])]});}
            var Q7;
            {var subQ0=sQuery(id+"F38.wireOp",EDGE,"E82.1.3");Q7=makeQuery(id+"F38.imprint","IMPRINT",FACE,{"disambiguationData":[TD([[makeQuery(id+"F38.imprint","IMPRINT",EDGE,{"derivedFrom":subQ0}),-1.0]])]});}
            var Q8;
            {var subQ0=sQuery(id+"F38.wireOp",EDGE,"E82.2.4");Q8=makeQuery(id+"F38.imprint","IMPRINT",FACE,{"disambiguationData":[TD([[makeQuery(id+"F38.imprint","IMPRINT",EDGE,{"derivedFrom":subQ0}),-1.0]])]});}
            var Q9;
            {var subQ0=sQuery(id+"F38.wireOp",EDGE,"E82.2.1");Q9=makeQuery(id+"F38.imprint","IMPRINT",FACE,{"disambiguationData":[TD([[makeQuery(id+"F38.imprint","IMPRINT",EDGE,{"derivedFrom":subQ0}),-1.0]])]});}
            var Q10;
            {var subQ0=sQuery(id+"F38.wireOp",EDGE,"E82.2.2");Q10=makeQuery(id+"F38.imprint","IMPRINT",FACE,{"disambiguationData":[TD([[makeQuery(id+"F38.imprint","IMPRINT",EDGE,{"derivedFrom":subQ0}),-1.0]])]});}
            var Q11;
            {var subQ0=sQuery(id+"F38.wireOp",EDGE,"E82.2.3");Q11=makeQuery(id+"F38.imprint","IMPRINT",FACE,{"disambiguationData":[TD([[makeQuery(id+"F38.imprint","IMPRINT",EDGE,{"derivedFrom":subQ0}),-1.0]])]});}
            var Q12;
            {var subQ0=sQuery(id+"F38.wireOp",EDGE,"E82.3.4");Q12=makeQuery(id+"F38.imprint","IMPRINT",FACE,{"disambiguationData":[TD([[makeQuery(id+"F38.imprint","IMPRINT",EDGE,{"derivedFrom":subQ0}),-1.0]])]});}
            var Q13;
            {var subQ0=sQuery(id+"F38.wireOp",EDGE,"E82.3.1");Q13=makeQuery(id+"F38.imprint","IMPRINT",FACE,{"disambiguationData":[TD([[makeQuery(id+"F38.imprint","IMPRINT",EDGE,{"derivedFrom":subQ0}),-1.0]])]});}
            var Q14;
            {var subQ0=sQuery(id+"F38.wireOp",EDGE,"E82.3.2");Q14=makeQuery(id+"F38.imprint","IMPRINT",FACE,{"disambiguationData":[TD([[makeQuery(id+"F38.imprint","IMPRINT",EDGE,{"derivedFrom":subQ0}),-1.0]])]});}
            var Q15;
            {var subQ0=sQuery(id+"F38.wireOp",EDGE,"E82.3.3");Q15=makeQuery(id+"F38.imprint","IMPRINT",FACE,{"disambiguationData":[TD([[makeQuery(id+"F38.imprint","IMPRINT",EDGE,{"derivedFrom":subQ0}),-1.0]])]});}
            extrude(context, id + "F39", {"entities" : qUnion([Q0, Q1, Q2, Q3, Q4, Q5, Q6, Q7, Q8, Q9, Q10, Q11, Q12, Q13, Q14, Q15]), "operationType" : NewBodyOperationType.REMOVE, "oppositeDirection" : true, "depth" : 0.38 * mm, "offsetDistance" : 25.4 * mm});
        }
        {
            var Q0;
            Q0=makeQuery(id+"F1.opExtrude","CAP_EDGE",EDGE,{"disambiguationData":[OSD([sQuery(id+"F0.wireOp",EDGE,"E0.bottom")])],"isStart":true});
            var Q1;
            Q1=makeQuery(id+"F1.opExtrude","CAP_EDGE",EDGE,{"disambiguationData":[OSD([sQuery(id+"F0.wireOp",EDGE,"E0.left")])],"isStart":true});
            var Q2;
            Q2=makeQuery(id+"F1.opExtrude","CAP_EDGE",EDGE,{"disambiguationData":[OSD([sQuery(id+"F0.wireOp",EDGE,"E0.right")])],"isStart":true});
            var Q3;
            Q3=makeQuery(id+"F1.opExtrude","CAP_EDGE",EDGE,{"disambiguationData":[OSD([sQuery(id+"F0.wireOp",EDGE,"E0.top")])],"isStart":true});
            var Q4;
            Q4=makeQuery(id+"F1.opExtrude","CAP_EDGE",EDGE,{"disambiguationData":[OSD([sQuery(id+"F0.wireOp",EDGE,"E0.bottom")])],"isStart":false});
            var Q5;
            Q5=makeQuery(id+"F1.opExtrude","CAP_EDGE",EDGE,{"disambiguationData":[OSD([sQuery(id+"F0.wireOp",EDGE,"E0.left")])],"isStart":false});
            var Q6;
            Q6=makeQuery(id+"F1.opExtrude","CAP_EDGE",EDGE,{"disambiguationData":[OSD([sQuery(id+"F0.wireOp",EDGE,"E0.top")])],"isStart":false});
            var Q7;
            Q7=makeQuery(id+"F1.opExtrude","CAP_EDGE",EDGE,{"disambiguationData":[OSD([sQuery(id+"F0.wireOp",EDGE,"E0.right")])],"isStart":false});
            var Q8;
            Q8=makeQuery(id+"F1.opExtrude","SWEPT_EDGE",EDGE,{"disambiguationData":[OSD([sQuery(id+"F0.wireOp",EDGE,"E0.top"),sQuery(id+"F0.wireOp",EDGE,"E0.right")])]});
            var Q9;
            Q9=makeQuery(id+"F1.opExtrude","SWEPT_EDGE",EDGE,{"disambiguationData":[OSD([sQuery(id+"F0.wireOp",EDGE,"E0.bottom"),sQuery(id+"F0.wireOp",EDGE,"E0.right")])]});
            var Q10;
            Q10=makeQuery(id+"F1.opExtrude","SWEPT_EDGE",EDGE,{"disambiguationData":[OSD([sQuery(id+"F0.wireOp",EDGE,"E0.bottom"),sQuery(id+"F0.wireOp",EDGE,"E0.left")])]});
            var Q11;
            Q11=makeQuery(id+"F1.opExtrude","SWEPT_EDGE",EDGE,{"disambiguationData":[OSD([sQuery(id+"F0.wireOp",EDGE,"E0.top"),sQuery(id+"F0.wireOp",EDGE,"E0.left")])]});
            fillet(context, id + "F40", {"entities" : qUnion([Q0, Q1, Q2, Q3, Q4, Q5, Q6, Q7, Q8, Q9, Q10, Q11]), "radius" : 0.5 * mm, "tangentPropagation" : true, "allowEdgeOverflow" : false});
        }
    });
